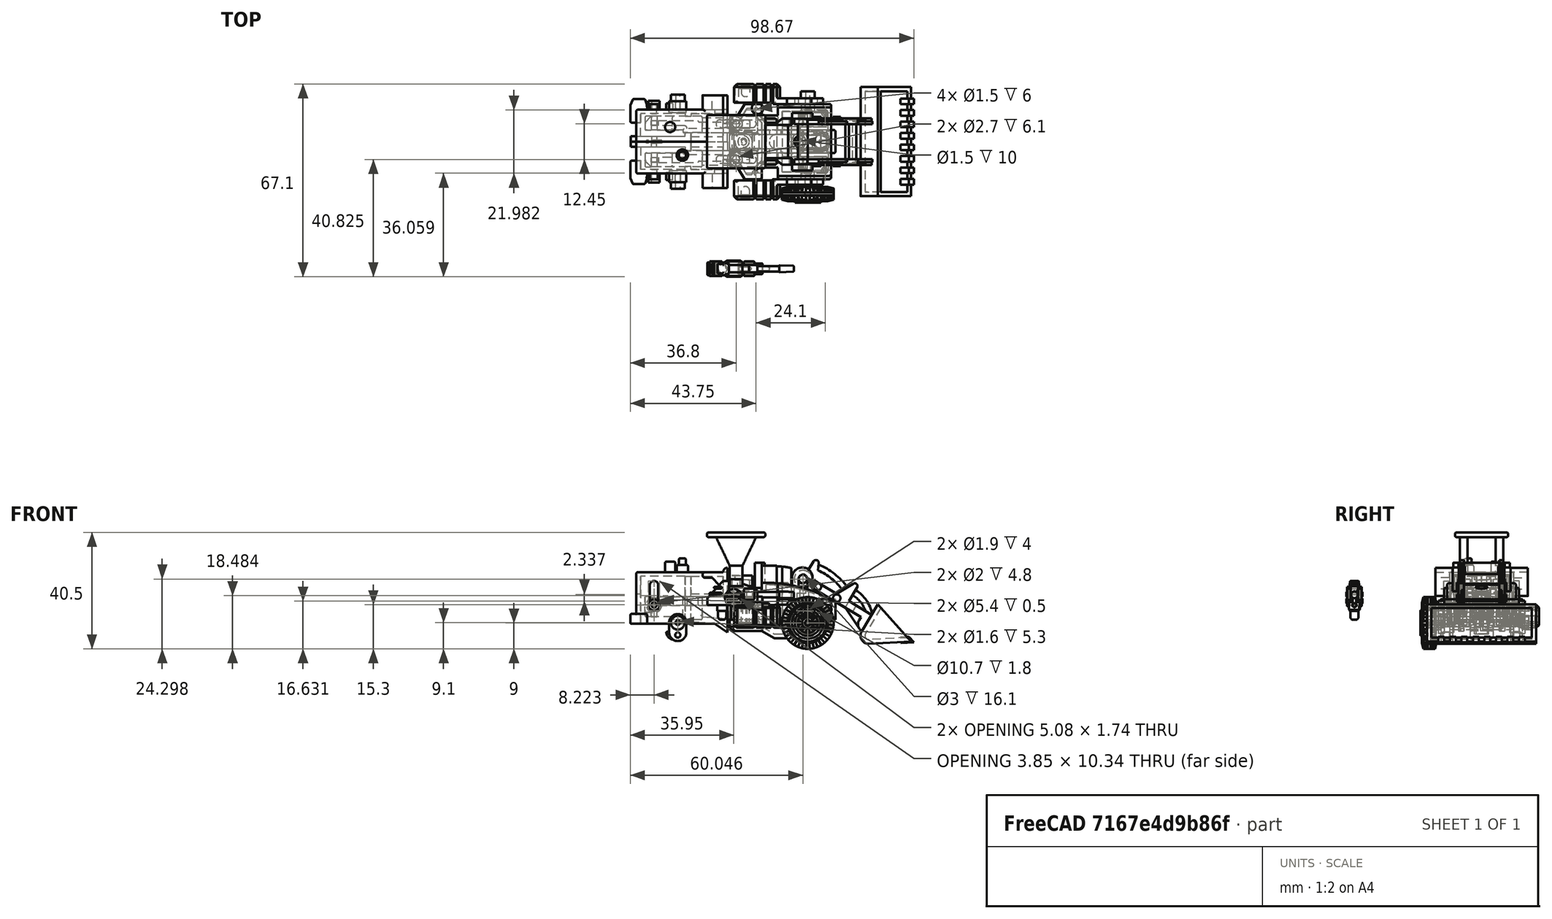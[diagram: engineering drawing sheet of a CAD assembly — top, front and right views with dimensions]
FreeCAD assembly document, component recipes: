
FREECAD ASSEMBLY — COMPONENT RECIPES ("Scrapper")

This assembly document has 14 components, labeled P0..P13 below (a component is one placed body or linked part). 14 of them carry a construction recipe — the FreeCAD feature program that regenerates the part from scratch, quoted from this document or its linked companion documents; the rest are supplied as boundary geometry only. No exploded tour is included for this assembly.
NOTE — document 3 of 4 of this assembly tour. The two overview renders and the header above are repeated from document 1; the component sections below continue where the previous document stopped.
COMPONENT P9 — recipe-attached ("Pre_Left_Arm", modeled in this document).
Construction recipe (the document's own serialized feature program — sketch geometry with constraints, then the solid features built on it; lengths are millimeters unless a unit is written):

FEATURE [Sketcher::SketchObject] Sketch077
  ArcFitTolerance = 1e-06
  AttachmentSupport = -> [XY_Plane002]
  FullyConstrained = true
  MakeInternals = false
  MapMode = 5
  sketch-geometry (20):
    g0: ArcOfCircle CenterX=-3.3 CenterY=1.7225 CenterZ=0 NormalX=0 NormalY=0 NormalZ=1 AngleXU=0 Radius=3.7225 StartAngle=3.62266 EndAngle=5.80212
    g1: ArcOfCircle CenterX=-6.6 CenterY=2 CenterZ=0 NormalX=0 NormalY=0 NormalZ=1 AngleXU=0 Radius=2 StartAngle=3.14159 EndAngle=4.71239
    g2: LineSegment StartX=-8.6 StartY=2 StartZ=0 EndX=-8.6 EndY=6 EndZ=0
    g3: ArcOfCircle CenterX=-6.6 CenterY=6 CenterZ=0 NormalX=0 NormalY=0 NormalZ=1 AngleXU=0 Radius=2 StartAngle=1.5708 EndAngle=3.14159
    g4: LineSegment StartX=-6.6 StartY=8 StartZ=0 EndX=-4.5 EndY=8 EndZ=0
    g5: LineSegment StartX=-4.5 StartY=8 StartZ=0 EndX=-4.5 EndY=8 EndZ=0
    g6: ArcOfCircle CenterX=-3 CenterY=8 CenterZ=0 NormalX=0 NormalY=0 NormalZ=1 AngleXU=0 Radius=1.5 StartAngle=1.5708 EndAngle=3.14159
    g7: LineSegment StartX=-3 StartY=9.5 StartZ=0 EndX=2.4 EndY=9.5 EndZ=0
    g8: ArcOfCircle CenterX=2.4 CenterY=8 CenterZ=0 NormalX=0 NormalY=0 NormalZ=1 AngleXU=0 Radius=1.5 StartAngle=0 EndAngle=1.5708
    g9: LineSegment StartX=3.9 StartY=8 StartZ=0 EndX=8.05 EndY=8 EndZ=0
    g10: ArcOfCircle CenterX=8.05 CenterY=7.25 CenterZ=0 NormalX=0 NormalY=0 NormalZ=1 AngleXU=0 Radius=0.75 StartAngle=4.71239 EndAngle=7.85398
    g11: LineSegment StartX=8.05 StartY=6.5 StartZ=0 EndX=8.05 EndY=1.5 EndZ=0
    g12: ArcOfCircle CenterX=8.05 CenterY=0.75 CenterZ=0 NormalX=0 NormalY=0 NormalZ=1 AngleXU=0 Radius=0.75 StartAngle=4.71239 EndAngle=7.85398
    g13: LineSegment StartX=8.05 StartY=0 StartZ=0 EndX=0 EndY=0 EndZ=0
    g14: LineSegment [constr] StartX=0 StartY=0 StartZ=0 EndX=0 EndY=-2 EndZ=0
    g15: LineSegment [constr] StartX=0 StartY=-2 StartZ=0 EndX=-6.6 EndY=-2 EndZ=0
    g16: LineSegment [constr] StartX=-6.6 StartY=0 StartZ=0 EndX=-6.6 EndY=-2 EndZ=0
    g17: LineSegment [constr] StartX=8.05 StartY=0 StartZ=0 EndX=8.8 EndY=0 EndZ=0
    g18: LineSegment [constr] StartX=8.8 StartY=0 StartZ=0 EndX=8.8 EndY=1.5 EndZ=0
    g19: LineSegment [constr] StartX=8.05 StartY=1.5 StartZ=0 EndX=8.8 EndY=1.5 EndZ=0
  constraints (65):
    c: Coincident(g0,g-1)
    c: PointOnObject(g0,g-1)
    c: Coincident(g1,g0)
    c: Coincident(g2,g1)
    c: Vertical(g2)
    c: Coincident(g3,g2)
    c: Coincident(g4,g3)
    c: Horizontal(g4)
    c: Coincident(g5,g4)
    c: Vertical(g5)
    c: Coincident(g6,g5)
    c: Coincident(g7,g6)
    c: Horizontal(g7)
    c: Coincident(g8,g7)
    c: Coincident(g9,g8)
    c: Horizontal(g9)
    c: Coincident(g10,g9)
    c: Coincident(g11,g10)
    c: Vertical(g11)
    c: Coincident(g12,g11)
    c: PointOnObject(g12,g-1)
    c: Coincident(g13,g12)
    c: Coincident(g13,g0)
    c: Diameter(g10) = 1.5
    c: Diameter(g12) = 1.5
    c: DistanceX(g11,g12) = 0
    c: DistanceX(g12,g12) = 0
    c: DistanceX(g9,g10) = 0
    c: DistanceX(g10,g10) = 0
    c: DistanceY(g11,g10) = 5
    c: DistanceY(g0,g6) = 9.5
    c: DistanceX(g7,g8) = 0
    c: DistanceY(g8,g8) = 0
    c: DistanceY(g5,g6) = 0
    c: DistanceX(g6,g6) = 0
    c: DistanceX(g0,g0) = 6.6
    c: DistanceX(g3,g3) = 0
    c: DistanceX(g1,g0) = 0
    c: DistanceY(g1,g1) = 0
    c: DistanceY(g3,g2) = 0
    c: DistanceY(g0,g3) = 8
    c: Radius(g6) = 1.5
    c: Radius(g3) = 2
    c: Radius(g1) = 2
    c: Coincident(g14,g0)
    c: PointOnObject(g14,g-2)
    c: Coincident(g15,g14)
    c: Horizontal(g15)
    c: Tangent(g15,g0)
    c: Coincident(g16,g0)
    c: Coincident(g16,g15)
    c: Vertical(g16)
    c: DistanceY(g14,g14) = 2
    c: DistanceX(g4,g8) = 8.4
    c: DistanceX(g2,g4) = 4.1
    c: DistanceX(g1,g11) = 16.65
    c: Coincident(g17,g12)
    c: PointOnObject(g17,g-1)
    c: Coincident(g18,g17)
    c: Coincident(g19,g11)
    c: Coincident(g19,g18)
    c: Horizontal(g19)
    c: Tangent(g18,g12)
    c: Vertical(g18)
    c: DistanceX(g0,g17) = 8.8
FEATURE [PartDesign::Pad] Pad049
  Direction = (0,0,1)
  Length = 2
  Length2 = 10
  Profile = -> Sketch077
  ReferenceAxis = -> Sketch077 [N_Axis]
  Refine = true
  Suppressed = false
  Type = 0
FEATURE [Sketcher::SketchObject] Sketch078
  ArcFitTolerance = 1e-06
  AttachmentSupport = -> [Pad049]
  ExternalGeometry = -> [Pad049]
  FullyConstrained = true
  MakeInternals = false
  MapMode = 5
  Placement = pos=(0,0,0) rot=(1,0,0;3.14159rad)
  sketch-geometry (1):
    g0: Circle CenterX=-3.3 CenterY=-1.7225 CenterZ=0 NormalX=0 NormalY=0 NormalZ=1 AngleXU=0 Radius=2.45
  constraints (2):
    c: Coincident(g0,g-3)
    c: Diameter(g0) = 4.9
FEATURE [PartDesign::Pad] Pad050
  BaseFeature = -> Pad049
  Direction = (0,0,-1)
  Length = 2.5
  Length2 = 10
  Profile = -> Sketch078
  ReferenceAxis = -> Sketch078 [N_Axis]
  Refine = true
  Suppressed = false
  Type = 0
FEATURE [Sketcher::SketchObject] Sketch079
  ArcFitTolerance = 1e-06
  AttachmentSupport = -> [Pad050]
  ExternalGeometry = -> [Pad050]
  FullyConstrained = true
  MakeInternals = false
  MapMode = 5
  Placement = pos=(0,0,-2.5) rot=(1,0,0;3.14159rad)
  sketch-geometry (1):
    g0: Circle CenterX=-3.3 CenterY=-1.7225 CenterZ=0 NormalX=0 NormalY=0 NormalZ=1 AngleXU=0 Radius=0.75
  constraints (2):
    c: Coincident(g0,g-4)
    c: Diameter(g0) = 1.5
FEATURE [PartDesign::Pocket] Pocket038
  BaseFeature = -> Pad050
  Direction = (0,0,1)
  Length = 5
  Length2 = 5
  Profile = -> Sketch079
  ReferenceAxis = -> Sketch079 [N_Axis]
  Refine = true
  Suppressed = false
  Type = 0
FEATURE [Sketcher::SketchObject] Sketch080
  ArcFitTolerance = 1e-06
  AttachmentSupport = -> [Pocket038]
  ExternalGeometry = -> [Pocket038]
  FullyConstrained = true
  MakeInternals = false
  MapMode = 5
  Placement = pos=(0,0,0) rot=(1,0,0;3.14159rad)
  sketch-geometry (8):
    g0: LineSegment StartX=6.35 StartY=-8 StartZ=0 EndX=22.35 EndY=-8 EndZ=0
    g1: LineSegment StartX=22.35 StartY=-8 StartZ=0 EndX=22.35 EndY=0 EndZ=0
    g2: LineSegment StartX=22.35 StartY=0 StartZ=0 EndX=6.35 EndY=0 EndZ=0
    g3: LineSegment StartX=6.35 StartY=0 StartZ=0 EndX=6.35 EndY=-8 EndZ=0
    g4: LineSegment StartX=20.85 StartY=-6.5 StartZ=0 EndX=20.85 EndY=-1.5 EndZ=0
    g5: LineSegment StartX=20.85 StartY=-1.5 StartZ=0 EndX=8.05 EndY=-1.5 EndZ=0
    g6: LineSegment StartX=8.05 StartY=-1.5 StartZ=0 EndX=8.05 EndY=-6.5 EndZ=0
    g7: LineSegment StartX=8.05 StartY=-6.5 StartZ=0 EndX=20.85 EndY=-6.5 EndZ=0
  constraints (24):
    c: Coincident(g0,g1)
    c: Coincident(g1,g2)
    c: Coincident(g2,g3)
    c: Coincident(g3,g0)
    c: Horizontal(g0)
    c: Horizontal(g2)
    c: Vertical(g1)
    c: Vertical(g3)
    c: PointOnObject(g0,g-3)
    c: PointOnObject(g1,g-1)
    c: DistanceX(g0,g0) = 16
    c: DistanceX(g-5,g0) = 14.3
    c: Coincident(g4,g5)
    c: Coincident(g5,g6)
    c: Coincident(g6,g7)
    c: Coincident(g7,g4)
    c: Vertical(g4)
    c: Vertical(g6)
    c: Horizontal(g5)
    c: Horizontal(g7)
    c: DistanceX(g4,g0) = 1.5
    c: DistanceY(g4,g1) = 1.5
    c: DistanceY(g4,g4) = 5
    c: Coincident(g6,g-5)
FEATURE [PartDesign::Pad] Pad051
  BaseFeature = -> Pocket038
  Direction = (0,0,-1)
  Length = 5
  Length2 = 10
  Profile = -> Sketch080
  ReferenceAxis = -> Sketch080 [N_Axis]
  Refine = true
  Suppressed = false
  Type = 0
FEATURE [PartDesign::Pad] Pad052
  BaseFeature = -> Pad051
  Direction = (0,0,-1)
  Length = 1.5
  Length2 = 10
  Profile = -> Sketch080
  ReferenceAxis = -> Sketch080 [N_Axis]
  Refine = true
  Reversed = true
  Suppressed = false
  Type = 0
FEATURE [Sketcher::SketchObject] Sketch081
  ArcFitTolerance = 1e-06
  AttachmentSupport = -> [Pad052]
  ExternalGeometry = -> [Pad052]
  FullyConstrained = true
  MakeInternals = false
  MapMode = 5
  Placement = pos=(0,0,-5) rot=(1,0,0;3.14159rad)
  sketch-geometry (4):
    g0: LineSegment StartX=8.05 StartY=-1.5 StartZ=0 EndX=8.05 EndY=-6.5 EndZ=0
    g1: LineSegment StartX=8.05 StartY=-6.5 StartZ=0 EndX=20.85 EndY=-6.5 EndZ=0
    g2: LineSegment StartX=20.85 StartY=-6.5 StartZ=0 EndX=20.85 EndY=-1.5 EndZ=0
    g3: LineSegment StartX=20.85 StartY=-1.5 StartZ=0 EndX=8.05 EndY=-1.5 EndZ=0
  constraints (10):
    c: Coincident(g0,g1)
    c: Coincident(g1,g2)
    c: Coincident(g2,g3)
    c: Coincident(g3,g0)
    c: Vertical(g0)
    c: Vertical(g2)
    c: Horizontal(g1)
    c: Horizontal(g3)
    c: Coincident(g0,g-5)
    c: Coincident(g1,g-6)
FEATURE [PartDesign::Pad] Pad053
  BaseFeature = -> Pad052
  Direction = (0,0,-1)
  Length = 1.5
  Length2 = 10
  Profile = -> Sketch081
  ReferenceAxis = -> Sketch081 [N_Axis]
  Refine = true
  Reversed = true
  Suppressed = false
  Type = 0
FEATURE [PartDesign::Chamfer] Chamfer
  Angle = 45
  Base = -> Pad053 [Edge11,Edge10,Edge40,Edge38,Edge54,Edge37,Edge36,Edge9]
  BaseFeature = -> Pad053
  ChamferType = 0
  FlipDirection = false
  Refine = true
  Size = 1
  Size2 = 1
  SupportTransform = false
  Suppressed = false
  UseAllEdges = false
FEATURE [Sketcher::SketchObject] Sketch082
  ArcFitTolerance = 1e-06
  AttachmentSupport = -> [Chamfer]
  ExternalGeometry = -> [Chamfer]
  FullyConstrained = true
  MakeInternals = false
  MapMode = 5
  Placement = pos=(0,0,-5) rot=(1,0,0;3.14159rad)
  sketch-geometry (8):
    g0: LineSegment StartX=8.8 StartY=0 StartZ=0 EndX=8.8 EndY=-8 EndZ=0
    g1: LineSegment StartX=8.8 StartY=-8 StartZ=0 EndX=9.6 EndY=-8 EndZ=0
    g2: LineSegment StartX=9.6 StartY=-8 StartZ=0 EndX=9.6 EndY=0 EndZ=0
    g3: LineSegment StartX=9.6 StartY=0 StartZ=0 EndX=8.8 EndY=0 EndZ=0
    g4: LineSegment StartX=11.3 StartY=0 StartZ=0 EndX=11.3 EndY=-8 EndZ=0
    g5: LineSegment StartX=11.3 StartY=-8 StartZ=0 EndX=12.1 EndY=-8 EndZ=0
    g6: LineSegment StartX=12.1 StartY=-8 StartZ=0 EndX=12.1 EndY=0 EndZ=0
    g7: LineSegment StartX=12.1 StartY=0 StartZ=0 EndX=11.3 EndY=0 EndZ=0
  constraints (24):
    c: Coincident(g0,g1)
    c: Coincident(g1,g2)
    c: Coincident(g2,g3)
    c: Coincident(g3,g0)
    c: Vertical(g0)
    c: Vertical(g2)
    c: Horizontal(g1)
    c: Horizontal(g3)
    c: PointOnObject(g0,g-4)
    c: PointOnObject(g1,g-5)
    c: Coincident(g4,g5)
    c: Coincident(g5,g6)
    c: Coincident(g6,g7)
    c: Coincident(g7,g4)
    c: Vertical(g4)
    c: Vertical(g6)
    c: Horizontal(g5)
    c: Horizontal(g7)
    c: PointOnObject(g4,g-4)
    c: PointOnObject(g5,g-5)
    c: DistanceX(g-3,g0) = 2.45
    c: DistanceX(g1,g4) = 1.7
    c: DistanceX(g1,g1) = 0.8
    c: DistanceX(g5,g5) = 0.8
FEATURE [PartDesign::Pocket] Pocket039
  BaseFeature = -> Chamfer
  Direction = (0,0,1)
  Length = 0.75
  Length2 = 5
  Profile = -> Sketch082
  ReferenceAxis = -> Sketch082 [N_Axis]
  Refine = true
  Suppressed = false
  Type = 0
FEATURE [Sketcher::SketchObject] Sketch083
  ArcFitTolerance = 1e-06
  AttachmentSupport = -> [Pocket039]
  ExternalGeometry = -> [Pocket039]
  FullyConstrained = true
  MakeInternals = false
  MapMode = 5
  Placement = pos=(0,0,0) rot=(1,0,0;1.5708rad)
  sketch-geometry (8):
    g0: LineSegment StartX=9.6 StartY=-4.25 StartZ=0 EndX=9.6 EndY=1.5 EndZ=0
    g1: LineSegment StartX=9.6 StartY=1.5 StartZ=0 EndX=8.8 EndY=1.5 EndZ=0
    g2: LineSegment StartX=8.8 StartY=1.5 StartZ=0 EndX=8.8 EndY=-4.25 EndZ=0
    g3: LineSegment StartX=8.8 StartY=-4.25 StartZ=0 EndX=9.6 EndY=-4.25 EndZ=0
    g4: LineSegment StartX=12.1 StartY=-4.25 StartZ=0 EndX=12.1 EndY=1.5 EndZ=0
    g5: LineSegment StartX=12.1 StartY=1.5 StartZ=0 EndX=11.3 EndY=1.5 EndZ=0
    g6: LineSegment StartX=11.3 StartY=1.5 StartZ=0 EndX=11.3 EndY=-4.25 EndZ=0
    g7: LineSegment StartX=11.3 StartY=-4.25 StartZ=0 EndX=12.1 EndY=-4.25 EndZ=0
  constraints (20):
    c: Coincident(g0,g1)
    c: Coincident(g1,g2)
    c: Coincident(g2,g3)
    c: Coincident(g3,g0)
    c: Vertical(g0)
    c: Vertical(g2)
    c: Horizontal(g1)
    c: Coincident(g0,g-4)
    c: PointOnObject(g1,g-3)
    c: Coincident(g4,g5)
    c: Coincident(g5,g6)
    c: Coincident(g6,g7)
    c: Coincident(g7,g4)
    c: Vertical(g4)
    c: Vertical(g6)
    c: Horizontal(g5)
    c: Coincident(g4,g-5)
    c: PointOnObject(g5,g-3)
    c: Coincident(g2,g-4)
    c: Coincident(g6,g-5)
FEATURE [PartDesign::Pocket] Pocket040
  BaseFeature = -> Pocket039
  Direction = (0,1,-2e-16)
  Length = 0.75
  Length2 = 5
  Profile = -> Sketch083
  ReferenceAxis = -> Sketch083 [N_Axis]
  Refine = true
  Suppressed = false
  Type = 0
FEATURE [Sketcher::SketchObject] Sketch084
  ArcFitTolerance = 1e-06
  AttachmentSupport = -> [Pocket040]
  ExternalGeometry = -> [Pocket040]
  FullyConstrained = true
  MakeInternals = false
  MapMode = 5
  Placement = pos=(0,8,0) rot=(0,0.707107,0.707107;3.14159rad)
  sketch-geometry (8):
    g0: LineSegment StartX=-8.8 StartY=-4.25 StartZ=0 EndX=-8.8 EndY=1.5 EndZ=0
    g1: LineSegment StartX=-8.8 StartY=1.5 StartZ=0 EndX=-9.6 EndY=1.5 EndZ=0
    g2: LineSegment StartX=-9.6 StartY=1.5 StartZ=0 EndX=-9.6 EndY=-4.25 EndZ=0
    g3: LineSegment StartX=-9.6 StartY=-4.25 StartZ=0 EndX=-8.8 EndY=-4.25 EndZ=0
    g4: LineSegment StartX=-11.3 StartY=-4.25 StartZ=0 EndX=-11.3 EndY=1.5 EndZ=0
    g5: LineSegment StartX=-11.3 StartY=1.5 StartZ=0 EndX=-12.1 EndY=1.5 EndZ=0
    g6: LineSegment StartX=-12.1 StartY=1.5 StartZ=0 EndX=-12.1 EndY=-4.25 EndZ=0
    g7: LineSegment StartX=-12.1 StartY=-4.25 StartZ=0 EndX=-11.3 EndY=-4.25 EndZ=0
  constraints (20):
    c: Coincident(g0,g1)
    c: Coincident(g1,g2)
    c: Coincident(g2,g3)
    c: Coincident(g3,g0)
    c: Vertical(g0)
    c: Vertical(g2)
    c: Horizontal(g1)
    c: Coincident(g0,g-3)
    c: PointOnObject(g1,g-5)
    c: Coincident(g4,g5)
    c: Coincident(g5,g6)
    c: Coincident(g6,g7)
    c: Coincident(g7,g4)
    c: Vertical(g4)
    c: Vertical(g6)
    c: Horizontal(g5)
    c: Coincident(g4,g-4)
    c: PointOnObject(g5,g-5)
    c: Coincident(g6,g-4)
    c: Coincident(g2,g-3)
FEATURE [PartDesign::Pocket] Pocket041
  BaseFeature = -> Pocket040
  Direction = (0,-1,2e-16)
  Length = 0.75
  Length2 = 5
  Profile = -> Sketch084
  ReferenceAxis = -> Sketch084 [N_Axis]
  Refine = true
  Suppressed = false
  Type = 0
FEATURE [Sketcher::SketchObject] Sketch085
  ArcFitTolerance = 1e-06
  AttachmentSupport = -> [Pocket041]
  ExternalGeometry = -> [Pocket041]
  FullyConstrained = true
  MakeInternals = false
  MapMode = 5
  Placement = pos=(0,0,1.5) rot=(0,0,1;0rad)
  sketch-geometry (6):
    g0: ArcOfCircle CenterX=8.05 CenterY=7.25 CenterZ=0 NormalX=0 NormalY=0 NormalZ=1 AngleXU=0 Radius=0.75 StartAngle=5.35e-14 EndAngle=1.5708
    g1: LineSegment StartX=8.05 StartY=8 StartZ=0 EndX=8.8 EndY=8 EndZ=0
    g2: LineSegment StartX=8.8 StartY=8 StartZ=0 EndX=8.8 EndY=7.25 EndZ=0
    g3: ArcOfCircle CenterX=8.05001 CenterY=0.749994 CenterZ=0 NormalX=0 NormalY=0 NormalZ=1 AngleXU=0 Radius=0.749994 StartAngle=4.71238 EndAngle=6.28319
    g4: LineSegment StartX=8.05 StartY=0 StartZ=0 EndX=8.8 EndY=0 EndZ=0
    g5: LineSegment StartX=8.8 StartY=0 StartZ=0 EndX=8.8 EndY=0.75 EndZ=0
  constraints (13):
    c: Tangent(g0,g-5) = -1.5708
    c: Coincident(g0,g-5)
    c: Coincident(g1,g0)
    c: Coincident(g1,g-4)
    c: Coincident(g2,g1)
    c: Coincident(g2,g0)
    c: Coincident(g3,g-8)
    c: Coincident(g3,g-7)
    c: Tangent(g3,g-6)
    c: Coincident(g4,g-8)
    c: Coincident(g5,g4)
    c: Coincident(g5,g-7)
    c: Coincident(g4,g-8)
FEATURE [PartDesign::Pocket] Pocket042
  BaseFeature = -> Pocket041
  Direction = (0,0,-1)
  Length = 7
  Length2 = 5
  Profile = -> Sketch085
  ReferenceAxis = -> Sketch085 [N_Axis]
  Refine = true
  Suppressed = false
  Type = 0
FEATURE [Sketcher::SketchObject] Sketch086
  ArcFitTolerance = 1e-06
  AttachmentSupport = -> [Pocket042]
  ExternalGeometry = -> [Pocket042]
  FullyConstrained = true
  MakeInternals = false
  MapMode = 5
  Placement = pos=(0,0,1.5) rot=(0,0,1;0rad)
  sketch-geometry (6):
    g0: LineSegment StartX=14.6 StartY=0 StartZ=0 EndX=15.1 EndY=0.75 EndZ=0
    g1: LineSegment StartX=15.1 StartY=0.75 StartZ=0 EndX=15.6 EndY=0 EndZ=0
    g2: LineSegment StartX=15.6 StartY=0 StartZ=0 EndX=14.6 EndY=0 EndZ=0
    g3: LineSegment StartX=14.6 StartY=8 StartZ=0 EndX=15.1 EndY=7.25 EndZ=0
    g4: LineSegment StartX=15.1 StartY=7.25 StartZ=0 EndX=15.6 EndY=8 EndZ=0
    g5: LineSegment StartX=15.6 StartY=8 StartZ=0 EndX=14.6 EndY=8 EndZ=0
  constraints (19):
    c: PointOnObject(g0,g-3)
    c: Coincident(g1,g0)
    c: PointOnObject(g1,g-3)
    c: Coincident(g2,g1)
    c: Coincident(g2,g0)
    c: DistanceX(g-3,g0) = 3
    c: DistanceY(g-4,g-4) = 0.75
    c: DistanceY(g0,g0) = 0.75
    c: DistanceX(g2,g2) = 1
    c: DistanceX(g0,g1) = 0.5
    c: PointOnObject(g3,g-5)
    c: Coincident(g4,g3)
    c: PointOnObject(g4,g-5)
    c: Coincident(g5,g4)
    c: Coincident(g5,g3)
    c: DistanceX(g-6,g3) = 3
    c: DistanceX(g5,g5) = 1
    c: DistanceY(g3,g4) = 0.75
    c: DistanceX(g3,g3) = 0.5
FEATURE [PartDesign::Pocket] Pocket043
  BaseFeature = -> Pocket042
  Direction = (0,0,-1)
  Length = 10
  Length2 = 5
  Profile = -> Sketch086
  ReferenceAxis = -> Sketch086 [N_Axis]
  Refine = true
  Suppressed = false
  Type = 0
FEATURE [Sketcher::SketchObject] Sketch087
  ArcFitTolerance = 1e-06
  AttachmentSupport = -> [Pocket043]
  ExternalGeometry = -> [Pocket043]
  FullyConstrained = true
  MakeInternals = false
  MapMode = 5
  Placement = pos=(0,8,0) rot=(0,0.707107,0.707107;3.14159rad)
  sketch-geometry (3):
    g0: LineSegment StartX=-14.6 StartY=-5 StartZ=0 EndX=-15.1 EndY=-4.25 EndZ=0
    g1: LineSegment StartX=-15.1 StartY=-4.25 StartZ=0 EndX=-15.6 EndY=-5 EndZ=0
    g2: LineSegment StartX=-15.6 StartY=-5 StartZ=0 EndX=-14.6 EndY=-5 EndZ=0
  constraints (9):
    c: PointOnObject(g0,g-3)
    c: PointOnObject(g0,g-6)
    c: Coincident(g1,g0)
    c: PointOnObject(g1,g-3)
    c: Coincident(g2,g1)
    c: Coincident(g2,g0)
    c: DistanceX(g2,g2) = 1
    c: DistanceX(g1,g-5) = 0
    c: DistanceY(g0,g0) = 0.75
FEATURE [PartDesign::Pocket] Pocket044
  BaseFeature = -> Pocket043
  Direction = (0,-1,2e-16)
  Length = 8
  Length2 = 5
  Profile = -> Sketch087
  ReferenceAxis = -> Sketch087 [N_Axis]
  Refine = true
  Suppressed = false
  Type = 0
FEATURE [Sketcher::SketchObject] Sketch088
  ArcFitTolerance = 1e-06
  AttachmentSupport = -> [Pocket044]
  ExternalGeometry = -> [Pocket044]
  FullyConstrained = true
  MakeInternals = false
  MapMode = 5
  Placement = pos=(0,0,0) rot=(1,0,0;1.5708rad)
  sketch-geometry (4):
    g0: LineSegment StartX=19.85 StartY=-5 StartZ=0 EndX=16.95 EndY=-5 EndZ=0
    g1: LineSegment StartX=16.95 StartY=-5 StartZ=0 EndX=16.95 EndY=-2.05 EndZ=0
    g2: LineSegment StartX=19.85 StartY=-5 StartZ=0 EndX=19.85 EndY=-2.05 EndZ=0
    g3: ArcOfCircle CenterX=18.4 CenterY=-2.05 CenterZ=0 NormalX=0 NormalY=0 NormalZ=1 AngleXU=0 Radius=1.45 StartAngle=0 EndAngle=3.14159
  constraints (13):
    c: PointOnObject(g0,g-3)
    c: PointOnObject(g0,g-3)
    c: Coincident(g1,g0)
    c: Vertical(g1)
    c: Coincident(g2,g0)
    c: Vertical(g2)
    c: Coincident(g3,g2)
    c: Coincident(g3,g1)
    c: DistanceX(g0,g-4) = 2.5
    c: Radius(g3) = 1.45
    c: DistanceY(g0,g3) = 2.95
    c: DistanceY(g3,g1) = 0
    c: DistanceY(g3,g2) = 0
FEATURE [PartDesign::Pocket] Pocket045
  BaseFeature = -> Pocket044
  Direction = (0,1,-2e-16)
  Length = 1.5
  Length2 = 5
  Profile = -> Sketch088
  ReferenceAxis = -> Sketch088 [N_Axis]
  Refine = true
  Suppressed = false
  Type = 0
FEATURE [Sketcher::SketchObject] Sketch089
  ArcFitTolerance = 1e-06
  AttachmentSupport = -> [Pocket045]
  ExternalGeometry = -> [Pocket045]
  FullyConstrained = true
  MakeInternals = false
  MapMode = 5
  Placement = pos=(22.35,0,0) rot=(0.57735,0.57735,0.57735;2.0944rad)
  sketch-geometry (12):
    g0: LineSegment StartX=1.85 StartY=1.5 StartZ=0 EndX=1.85 EndY=-5 EndZ=0
    g1: LineSegment StartX=1.85 StartY=-5 StartZ=0 EndX=2.05 EndY=-5 EndZ=0
    g2: LineSegment StartX=2.05 StartY=-5 StartZ=0 EndX=2.05 EndY=1.5 EndZ=0
    g3: LineSegment StartX=2.05 StartY=1.5 StartZ=0 EndX=1.85 EndY=1.5 EndZ=0
    g4: LineSegment StartX=3.9 StartY=1.5 StartZ=0 EndX=3.9 EndY=-5 EndZ=0
    g5: LineSegment StartX=3.9 StartY=-5 StartZ=0 EndX=4.1 EndY=-5 EndZ=0
    g6: LineSegment StartX=4.1 StartY=-5 StartZ=0 EndX=4.1 EndY=1.5 EndZ=0
    g7: LineSegment StartX=4.1 StartY=1.5 StartZ=0 EndX=3.9 EndY=1.5 EndZ=0
    g8: LineSegment StartX=5.95 StartY=1.5 StartZ=0 EndX=5.95 EndY=-5 EndZ=0
    g9: LineSegment StartX=5.95 StartY=-5 StartZ=0 EndX=6.15 EndY=-5 EndZ=0
    g10: LineSegment StartX=6.15 StartY=-5 StartZ=0 EndX=6.15 EndY=1.5 EndZ=0
    g11: LineSegment StartX=6.15 StartY=1.5 StartZ=0 EndX=5.95 EndY=1.5 EndZ=0
  constraints (38):
    c: DistanceX(g-4,g-3) = 8
    c: Coincident(g0,g1)
    c: Coincident(g1,g2)
    c: Coincident(g2,g3)
    c: Coincident(g3,g0)
    c: Vertical(g0)
    c: Vertical(g2)
    c: Horizontal(g1)
    c: Horizontal(g3)
    c: PointOnObject(g0,g-5)
    c: PointOnObject(g1,g-6)
    c: Coincident(g4,g5)
    c: Coincident(g5,g6)
    c: Coincident(g6,g7)
    c: Coincident(g7,g4)
    c: Vertical(g4)
    c: Vertical(g6)
    c: Horizontal(g5)
    c: Horizontal(g7)
    c: PointOnObject(g4,g-5)
    c: PointOnObject(g5,g-6)
    c: Coincident(g8,g9)
    c: Coincident(g9,g10)
    c: Coincident(g10,g11)
    c: Coincident(g11,g8)
    c: Vertical(g8)
    c: Vertical(g10)
    c: Horizontal(g9)
    c: Horizontal(g11)
    c: PointOnObject(g8,g-5)
    c: PointOnObject(g9,g-6)
    c: DistanceX(g-4,g0) = 1.85
    c: DistanceX(g2,g4) = 1.85
    c: DistanceX(g3,g3) = 0.2
    c: DistanceX(g7,g7) = 0.2
    c: DistanceX(g11,g11) = 0.2
    c: DistanceX(g6,g8) = 1.85
    c: DistanceX(g10,g-3) = 1.85
FEATURE [PartDesign::Pocket] Pocket046
  BaseFeature = -> Pocket045
  Direction = (-1,0,0)
  Length = 0.3
  Length2 = 5
  Profile = -> Sketch089
  ReferenceAxis = -> Sketch089 [N_Axis]
  Refine = true
  Suppressed = false
  Type = 0
FEATURE [PartDesign::Fillet] Fillet005
  Base = -> Pocket046 [Edge32,Edge34,Edge88,Edge93,Edge36,Edge38,Edge96,Edge101,Edge40,Edge42,Edge104,Edge68,Edge109,Edge106,Edge102,Edge98,Edge94,Edge90]
  BaseFeature = -> Pocket046
  Radius = 0.2
  Refine = true
  SupportTransform = false
  Suppressed = false
  UseAllEdges = false
FEATURE [PartDesign::Fillet] Fillet006
  Base = -> Fillet005 [Edge19,Edge11,Edge5,Edge40,Edge46,Edge39]
  BaseFeature = -> Fillet005
  Radius = 0.5
  Refine = true
  SupportTransform = false
  Suppressed = false
  UseAllEdges = false
FEATURE [PartDesign::Fillet] Fillet007
  Base = -> Fillet006 [Edge1,Edge3,Edge15,Edge27,Edge39,Edge41]
  BaseFeature = -> Fillet006
  Radius = 0.19
  Refine = true
  SupportTransform = false
  Suppressed = false
  UseAllEdges = false
FEATURE [Sketcher::SketchObject] Sketch090
  ArcFitTolerance = 1e-06
  AttachmentSupport = -> [Fillet007]
  ExternalGeometry = -> [Fillet007]
  FullyConstrained = true
  MakeInternals = false
  MapMode = 5
  Placement = pos=(0,0,2) rot=(0,0,1;0rad)
  sketch-geometry (3):
    g0: Circle CenterX=-3.3 CenterY=5.9 CenterZ=0 NormalX=0 NormalY=0 NormalZ=1 AngleXU=0 Radius=2.2
    g1: LineSegment [constr] StartX=-5.5 StartY=8 StartZ=0 EndX=-5.5 EndY=4 EndZ=0
    g2: LineSegment [constr] StartX=-5.5 StartY=8.1 StartZ=0 EndX=0.5 EndY=8.1 EndZ=0
  constraints (11):
    c: Diameter(g0) = 4.4
    c: Vertical(g1)
    c: PointOnObject(g1,g-4)
    c: DistanceY(g1,g1) = 4
    c: Tangent(g1,g0)
    c: PointOnObject(g2,g1)
    c: Horizontal(g2)
    c: DistanceY(g2,g-5) = 1.4
    c: DistanceX(g2,g2) = 6
    c: Tangent(g0,g2)
    c: DistanceX(g0,g-7) = 0
FEATURE [PartDesign::Pad] Pad054
  BaseFeature = -> Fillet007
  Direction = (0,0,1)
  Length = 5.5
  Length2 = 10
  Profile = -> Sketch090
  ReferenceAxis = -> Sketch090 [N_Axis]
  Refine = true
  Suppressed = false
  Type = 0
FEATURE [Sketcher::SketchObject] Sketch091
  ArcFitTolerance = 1e-06
  AttachmentSupport = -> [Pad054]
  ExternalGeometry = -> [Pad054]
  FullyConstrained = true
  MakeInternals = false
  MapMode = 5
  Placement = pos=(0,0,7.5) rot=(0,0,1;0rad)
  sketch-geometry (1):
    g0: Circle CenterX=-3.3 CenterY=5.9 CenterZ=0 NormalX=0 NormalY=0 NormalZ=1 AngleXU=0 Radius=0.95
  constraints (2):
    c: Coincident(g0,g-3)
    c: Diameter(g0) = 1.9
FEATURE [PartDesign::Pocket] Pocket047
  BaseFeature = -> Pad054
  Direction = (0,0,-1)
  Length = 5.5
  Length2 = 5
  Profile = -> Sketch091
  ReferenceAxis = -> Sketch091 [N_Axis]
  Refine = true
  Suppressed = false
  Type = 0
FEATURE [Sketcher::SketchObject] Sketch092
  ArcFitTolerance = 1e-06
  AttachmentOffset = pos=(0,0,-1.6) rot=(0,0,1;0rad)
  AttachmentSupport = -> [Pocket047]
  ExternalGeometry = -> [Pocket047]
  FullyConstrained = true
  MakeInternals = false
  MapMode = 5
  Placement = pos=(0,0,5.9) rot=(0,0,1;0rad)
  sketch-geometry (4):
    g0: LineSegment StartX=-1.31569 StartY=6.85 StartZ=0 EndX=-1.1 EndY=6.85 EndZ=0
    g1: LineSegment StartX=-1.31569 StartY=4.95 StartZ=0 EndX=-1.1 EndY=4.95 EndZ=0
    g2: ArcOfCircle CenterX=-1.1 CenterY=5.9 CenterZ=0 NormalX=0 NormalY=0 NormalZ=1 AngleXU=0 Radius=0.95 StartAngle=4.71239 EndAngle=7.85398
    g3: ArcOfCircle CenterX=-3.3 CenterY=5.9 CenterZ=0 NormalX=0 NormalY=0 NormalZ=1 AngleXU=0 Radius=2.2 StartAngle=5.83668 EndAngle=6.72969
  constraints (13):
    c: PointOnObject(g0,g-4)
    c: Horizontal(g0)
    c: PointOnObject(g1,g-4)
    c: Horizontal(g1)
    c: Coincident(g2,g0)
    c: Coincident(g2,g1)
    c: DistanceX(g2,g2) = 0
    c: DistanceX(g1,g2) = 0
    c: Diameter(g2) = 1.9
    c: Coincident(g3,g0)
    c: Coincident(g3,g1)
    c: PointOnObject(g-3,g3)
    c: Coincident(g2,g-3)
FEATURE [PartDesign::Pad] Pad055
  BaseFeature = -> Pocket047
  Direction = (0,0,1)
  Length = 1.3
  Length2 = 10
  Profile = -> Sketch092
  ReferenceAxis = -> Sketch092 [N_Axis]
  Refine = true
  Reversed = true
  Suppressed = false
  Type = 0
FEATURE [Sketcher::SketchObject] Sketch093
  ArcFitTolerance = 1e-06
  AttachmentSupport = -> [Pad055]
  ExternalGeometry = -> [Pad055]
  FullyConstrained = true
  MakeInternals = false
  MapMode = 5
  Placement = pos=(0,0,2) rot=(0,0,1;0rad)
  sketch-geometry (1):
    g0: Circle CenterX=-0.6 CenterY=5.9 CenterZ=0 NormalX=0 NormalY=0 NormalZ=1 AngleXU=0 Radius=1.8
  constraints (4):
    c: Diameter(g0) = 3.6
    c: Diameter(g-6) = 4.4
    c: DistanceY(g0,g-4) = 0
    c: DistanceX(g-4,g0) = 0.5
FEATURE [PartDesign::Pocket] Pocket048
  BaseFeature = -> Pad055
  Direction = (0,0,-1)
  Length = 5
  Length2 = 5
  Profile = -> Sketch093
  ReferenceAxis = -> Sketch093 [N_Axis]
  Refine = true
  Suppressed = false
  Type = 0
FEATURE [Sketcher::SketchObject] Sketch094
  ArcFitTolerance = 1e-06
  AttachmentSupport = -> [Pocket048]
  ExternalGeometry = -> [Pocket048]
  FullyConstrained = true
  MakeInternals = false
  MapMode = 5
  Placement = pos=(0,0,2) rot=(0,0,1;0rad)
  sketch-geometry (1):
    g0: Circle CenterX=-3.3 CenterY=5.9 CenterZ=0 NormalX=0 NormalY=0 NormalZ=1 AngleXU=0 Radius=0.95
  constraints (2):
    c: Coincident(g0,g-3)
    c: Equal(g0,g-3)
FEATURE [PartDesign::Pad] Pad056
  BaseFeature = -> Pocket048
  Direction = (0,0,1)
  Length = 1.5
  Length2 = 10
  Profile = -> Sketch094
  ReferenceAxis = -> Sketch094 [N_Axis]
  Refine = true
  Suppressed = false
  Type = 0
FEATURE [Sketcher::SketchObject] Sketch095
  ArcFitTolerance = 1e-06
  AttachmentSupport = -> [Pad056]
  ExternalGeometry = -> [Pad056]
  FullyConstrained = true
  MakeInternals = false
  MapMode = 5
  Placement = pos=(0,0,2) rot=(1,0,0;3.14159rad)
  sketch-geometry (4):
    g0: LineSegment StartX=-1.10911 StartY=-6.1 StartZ=0 EndX=-1.05411 EndY=-6.1 EndZ=0
    g1: LineSegment StartX=-1.05411 StartY=-6.1 StartZ=0 EndX=-1.05411 EndY=-5.7 EndZ=0
    g2: LineSegment StartX=-1.05411 StartY=-5.7 StartZ=0 EndX=-1.10911 EndY=-5.7 EndZ=0
    g3: ArcOfCircle CenterX=-3.3 CenterY=-5.9 CenterZ=0 NormalX=0 NormalY=0 NormalZ=1 AngleXU=0 Radius=2.2 StartAngle=6.19215 EndAngle=6.37422
  constraints (13):
    c: PointOnObject(g0,g-4)
    c: Horizontal(g0)
    c: Coincident(g1,g0)
    c: Vertical(g1)
    c: Coincident(g2,g1)
    c: PointOnObject(g2,g-3)
    c: Horizontal(g2)
    c: DistanceY(g-4,g2) = 0.2
    c: DistanceY(g0,g-4) = 0.2
    c: DistanceX(g0,g0) = 0.055
    c: Coincident(g3,g2)
    c: Coincident(g3,g0)
    c: PointOnObject(g-4,g3)
FEATURE [PartDesign::Body] Body002  label="Right_Arm"
  AllowCompound = false
  Group = -> [Sketch077,Pad049,Sketch078,Pad050,Sketch079,Pocket038,Sketch080,Pad051,Pad052,Sketch081,Pad053,Chamfer,Sketch082,Pocket039,Sketch083,Pocket040,Sketch084,Pocket041,Sketch085,Pocket042,Sketch086,Pocket043,Sketch087,Pocket044,Sketch088,Pocket045,Sketch089,Pocket046,Fillet005,Fillet006,Fillet007,Sketch090,Pad054,Sketch091,Pocket047,Sketch092,Pad055,Sketch093,Pocket048,Sketch094,Pad056,Sketch095,+13 more]
  Origin = -> Origin002
  Placement = pos=(-11.4,-15.05,-7.9) rot=(0,-0.71,-0.71;3.14159rad)
  Tip = -> Pocket141
COMPONENT P10 — recipe-attached ("Tire2", modeled in this document).
Construction recipe (the document's own serialized feature program — sketch geometry with constraints, then the solid features built on it; lengths are millimeters unless a unit is written):

FEATURE [Sketcher::SketchObject] Sketch235
  ArcFitTolerance = 1e-06
  AttachmentSupport = -> [XZ_Plane007]
  FullyConstrained = true
  MakeInternals = false
  MapMode = 5
  Placement = pos=(0,0,0) rot=(1,0,0;1.5708rad)
  sketch-geometry (1):
    g0: Circle CenterX=0 CenterY=0 CenterZ=0 NormalX=0 NormalY=0 NormalZ=1 AngleXU=0 Radius=4.5
  constraints (2):
    c: Coincident(g0,g-1)
    c: Diameter(g0) = 9
FEATURE [PartDesign::Pad] Pad145
  Direction = (0,-1,2e-16)
  Length = 5.5
  Length2 = 10
  Placement = pos=(0,0,0) rot=(1,0,0;1.5708rad)
  Profile = -> Sketch235
  ReferenceAxis = -> Sketch235 [N_Axis]
  Refine = true
  Suppressed = false
  Type = 0
FEATURE [Sketcher::SketchObject] Sketch236
  ArcFitTolerance = 1e-06
  AttachmentSupport = -> [Pad145]
  FullyConstrained = true
  MakeInternals = false
  MapMode = 5
  Placement = pos=(0,-5.5,0) rot=(1,0,0;1.5708rad)
  sketch-geometry (1):
    g0: Circle CenterX=0 CenterY=0 CenterZ=0 NormalX=0 NormalY=0 NormalZ=1 AngleXU=0 Radius=3.5
  constraints (2):
    c: Coincident(g0,g-1)
    c: Diameter(g0) = 7
FEATURE [PartDesign::Pocket] Pocket097
  BaseFeature = -> Pad145
  Direction = (0,1,-2e-16)
  Length = 0.5
  Length2 = 5
  Placement = pos=(0,0,0) rot=(1,0,0;1.5708rad)
  Profile = -> Sketch236
  ReferenceAxis = -> Sketch236 [N_Axis]
  Refine = true
  Suppressed = false
  Type = 0
FEATURE [Sketcher::SketchObject] Sketch237
  ArcFitTolerance = 1e-06
  AttachmentSupport = -> [Pocket097]
  FullyConstrained = true
  MakeInternals = false
  MapMode = 5
  Placement = pos=(0,-5,1.4e-15) rot=(1,0,0;1.5708rad)
  sketch-geometry (1):
    g0: Circle CenterX=0 CenterY=0 CenterZ=0 NormalX=0 NormalY=0 NormalZ=1 AngleXU=0 Radius=0.75
  constraints (2):
    c: Coincident(g0,g-1)
    c: Diameter(g0) = 1.5
FEATURE [PartDesign::Pocket] Pocket098
  BaseFeature = -> Pocket097
  Direction = (0,1,-2e-16)
  Length = 5
  Length2 = 5
  Placement = pos=(0,0,0) rot=(1,0,0;1.5708rad)
  Profile = -> Sketch237
  ReferenceAxis = -> Sketch237 [N_Axis]
  Refine = true
  Suppressed = false
  Type = 0
FEATURE [Sketcher::SketchObject] Sketch238
  ArcFitTolerance = 1e-06
  AttachmentSupport = -> [Pocket098]
  FullyConstrained = true
  MakeInternals = false
  MapMode = 5
  Placement = pos=(0,-5,1.4e-15) rot=(1,0,0;1.5708rad)
  sketch-geometry (1):
    g0: Circle CenterX=0 CenterY=0 CenterZ=0 NormalX=0 NormalY=0 NormalZ=1 AngleXU=0 Radius=2
  constraints (2):
    c: Coincident(g0,g-1)
    c: Diameter(g0) = 4
FEATURE [PartDesign::Pocket] Pocket099
  BaseFeature = -> Pocket098
  Direction = (0,1,-2e-16)
  Length = 1.5
  Length2 = 5
  Placement = pos=(0,0,0) rot=(1,0,0;1.5708rad)
  Profile = -> Sketch238
  ReferenceAxis = -> Sketch238 [N_Axis]
  Refine = true
  Suppressed = false
  Type = 0
FEATURE [Sketcher::SketchObject] Sketch239
  ArcFitTolerance = 1e-06
  AttachmentSupport = -> [Pocket099]
  FullyConstrained = true
  MakeInternals = false
  MapMode = 5
  Placement = pos=(0,-5,1.4e-15) rot=(1,0,0;1.5708rad)
  sketch-geometry (12):
    g0: Circle CenterX=0 CenterY=2.75 CenterZ=0 NormalX=0 NormalY=0 NormalZ=1 AngleXU=0 Radius=0.5
    g1: Circle CenterX=2.75 CenterY=0 CenterZ=0 NormalX=0 NormalY=0 NormalZ=1 AngleXU=0 Radius=0.5
    g2: Circle CenterX=0 CenterY=-2.75 CenterZ=0 NormalX=0 NormalY=0 NormalZ=1 AngleXU=0 Radius=0.5
    g3: Circle CenterX=-2.75 CenterY=0 CenterZ=0 NormalX=0 NormalY=0 NormalZ=1 AngleXU=0 Radius=0.5
    g4: Circle CenterX=-1.94454 CenterY=1.94454 CenterZ=0 NormalX=0 NormalY=0 NormalZ=1 AngleXU=0 Radius=0.5
    g5: Circle CenterX=1.94454 CenterY=1.94454 CenterZ=0 NormalX=0 NormalY=0 NormalZ=1 AngleXU=0 Radius=0.5
    g6: Circle CenterX=1.94454 CenterY=-1.94454 CenterZ=0 NormalX=0 NormalY=0 NormalZ=1 AngleXU=0 Radius=0.5
    g7: Circle CenterX=-1.94454 CenterY=-1.94454 CenterZ=0 NormalX=0 NormalY=0 NormalZ=1 AngleXU=0 Radius=0.5
    g8: LineSegment [constr] StartX=0 StartY=0 StartZ=0 EndX=-1.94454 EndY=1.94454 EndZ=0
    g9: LineSegment [constr] StartX=0 StartY=0 StartZ=0 EndX=1.94454 EndY=1.94454 EndZ=0
    g10: LineSegment [constr] StartX=0 StartY=0 StartZ=0 EndX=1.94454 EndY=-1.94454 EndZ=0
    g11: LineSegment [constr] StartX=0 StartY=0 StartZ=0 EndX=-1.94454 EndY=-1.94454 EndZ=0
  constraints (32):
    c: PointOnObject(g0,g-2)
    c: PointOnObject(g1,g-1)
    c: PointOnObject(g2,g-2)
    c: PointOnObject(g3,g-1)
    c: Diameter(g0) = 1
    c: Diameter(g5) = 1
    c: Diameter(g1) = 1
    c: Diameter(g6) = 1
    c: Diameter(g2) = 1
    c: Diameter(g7) = 1
    c: Diameter(g4) = 1
    c: Diameter(g3) = 1
    c: Distance(g-1,g1) = 2.75
    c: Distance(g-1,g0) = 2.75
    c: Distance(g-1,g3) = 2.75
    c: Distance(g-1,g2) = 2.75
    c: Distance(g-1,g6) = 2.75
    c: Distance(g-1,g7) = 2.75
    c: Distance(g-1,g4) = 2.75
    c: Distance(g-1,g5) = 2.75
    c: Coincident(g8,g-1)
    c: Coincident(g8,g4)
    c: Coincident(g9,g8)
    c: Coincident(g9,g5)
    c: Coincident(g10,g8)
    c: Coincident(g10,g6)
    c: Coincident(g11,g8)
    c: Coincident(g11,g7)
    c: Angle(g-2,g8) = 0.785398
    c: Angle(g9,g-2) = 0.785398
    c: Angle(g10,g-1) = 0.785398
    c: Angle(g11,g-1) = 2.35619
FEATURE [PartDesign::Pad] Pad146
  BaseFeature = -> Pocket099
  Direction = (0,-1,2e-16)
  Length = 0.5
  Length2 = 10
  Placement = pos=(0,0,0) rot=(1,0,0;1.5708rad)
  Profile = -> Sketch239
  ReferenceAxis = -> Sketch239 [N_Axis]
  Refine = true
  Suppressed = false
  Type = 0
FEATURE [Sketcher::SketchObject] Sketch240
  ArcFitTolerance = 1e-06
  AttachmentOffset = pos=(0,0,-1) rot=(0,0,1;0rad)
  AttachmentSupport = -> [Pad146]
  ExternalGeometry = -> [Pad146]
  FullyConstrained = true
  MakeInternals = false
  MapMode = 5
  Placement = pos=(0,-4.5,-2e-16) rot=(1,0,0;1.5708rad)
  sketch-geometry (2):
    g0: Circle CenterX=0 CenterY=0 CenterZ=0 NormalX=0 NormalY=0 NormalZ=1 AngleXU=0 Radius=5.5
    g1: Circle CenterX=0 CenterY=0 CenterZ=0 NormalX=0 NormalY=0 NormalZ=1 AngleXU=0 Radius=4.50001
  constraints (4):
    c: Coincident(g0,g-1)
    c: Coincident(g1,g0)
    c: Diameter(g0) = 11
    c: Tangent(g1,g-3)
FEATURE [PartDesign::Pad] Pad147
  BaseFeature = -> Pad146
  Direction = (0,-1,2e-16)
  Length = 4.5
  Length2 = 10
  Placement = pos=(0,0,0) rot=(1,0,0;1.5708rad)
  Profile = -> Sketch240
  ReferenceAxis = -> Sketch240 [N_Axis]
  Refine = true
  Reversed = true
  Suppressed = false
  Type = 0
FEATURE [Sketcher::SketchObject] Sketch241
  ArcFitTolerance = 1e-06
  AttachmentSupport = -> [Pad147]
  ExternalGeometry = -> [Pad147]
  FullyConstrained = true
  MakeInternals = false
  MapMode = 5
  Placement = pos=(0,-5,1.4e-15) rot=(1,0,0;1.5708rad)
  sketch-geometry (2):
    g0: Circle CenterX=0 CenterY=0 CenterZ=0 NormalX=0 NormalY=0 NormalZ=1 AngleXU=0 Radius=5.50001
    g1: Circle CenterX=0 CenterY=0 CenterZ=0 NormalX=0 NormalY=0 NormalZ=1 AngleXU=0 Radius=9
  constraints (4):
    c: Coincident(g0,g-1)
    c: Coincident(g1,g0)
    c: Diameter(g1) = 18
    c: Tangent(g0,g-3)
FEATURE [PartDesign::Pad] Pad148
  BaseFeature = -> Pad147
  Direction = (0,-1,2e-16)
  Length = 5
  Length2 = 10
  Placement = pos=(0,0,0) rot=(1,0,0;1.5708rad)
  Profile = -> Sketch241
  ReferenceAxis = -> Sketch241 [N_Axis]
  Refine = true
  Reversed = true
  Suppressed = false
  Type = 0
FEATURE [Sketcher::SketchObject] Sketch242
  ArcFitTolerance = 1e-06
  AttachmentOffset = pos=(3,0,0) rot=(0,0,1;0rad)
  AttachmentSupport = -> [YZ_Plane007]
  ExternalGeometry = -> [Pad148]
  FullyConstrained = true
  MakeInternals = false
  MapMode = 5
  Placement = pos=(0,3,0) rot=(0.57735,0.57735,0.57735;2.0944rad)
  sketch-geometry (4):
    g0: LineSegment StartX=-8 StartY=6.5 StartZ=0 EndX=-7.5 EndY=5.5 EndZ=0
    g1: LineSegment StartX=-7.5 StartY=5.5 StartZ=0 EndX=-8.5 EndY=5.5 EndZ=0
    g2: LineSegment StartX=-8 StartY=6.5 StartZ=0 EndX=-8.5 EndY=6.5 EndZ=0
    g3: LineSegment StartX=-8.5 StartY=6.5 StartZ=0 EndX=-8.5 EndY=5.5 EndZ=0
  constraints (11):
    c: Coincident(g1,g0)
    c: Horizontal(g1)
    c: Coincident(g0,g-4)
    c: PointOnObject(g0,g-5)
    c: Coincident(g2,g0)
    c: Coincident(g3,g2)
    c: Coincident(g3,g1)
    c: Vertical(g3)
    c: Horizontal(g2)
    c: DistanceY(g0,g0) = 1
    c: DistanceX(g1,g1) = 1
FEATURE [PartDesign::SubtractivePipe] SubtractivePipe
  AuxilleryCurvelinear = true
  AuxillerySpineTangent = false
  BaseFeature = -> Pad148
  Binormal = (0,0,0)
  Mode = 0
  Placement = pos=(0,0,0) rot=(1,0,0;1.5708rad)
  Profile = -> Sketch242
  Refine = true
  Spine = -> Pad148 [Edge6]
  SpineTangent = false
  Suppressed = false
  Transformation = 0
  Transition = 0
FEATURE [PartDesign::Chamfer] Chamfer001
  Angle = 45
  Base = -> SubtractivePipe [Edge10,Edge21]
  BaseFeature = -> SubtractivePipe
  ChamferType = 0
  FlipDirection = false
  Placement = pos=(0,0,0) rot=(1,0,0;1.5708rad)
  Refine = true
  Size = 1.99
  Size2 = 1
  SupportTransform = false
  Suppressed = false
  UseAllEdges = false
FEATURE [Sketcher::SketchObject] Sketch243
  ArcFitTolerance = 1e-06
  AttachmentSupport = -> [Chamfer001]
  ExternalGeometry = -> [Chamfer001]
  FullyConstrained = true
  MakeInternals = false
  MapMode = 5
  Placement = pos=(0,-5,0) rot=(1,0,0;1.5708rad)
  sketch-geometry (120):
    g0: LineSegment [constr] StartX=0 StartY=0 StartZ=0 EndX=-0.706132 EndY=8.97226 EndZ=0
    g1: LineSegment [constr] StartX=0 StartY=0 StartZ=0 EndX=-2.10101 EndY=8.75133 EndZ=0
    g2: LineSegment [constr] StartX=0 StartY=0 StartZ=0 EndX=-3.44415 EndY=8.31492 EndZ=0
    g3: LineSegment [constr] StartX=0 StartY=0 StartZ=0 EndX=-4.70249 EndY=7.67376 EndZ=0
    g4: LineSegment [constr] StartX=0 StartY=0 StartZ=0 EndX=-5.84503 EndY=6.84365 EndZ=0
    g5: LineSegment [constr] StartX=0 StartY=0 StartZ=0 EndX=-6.84365 EndY=5.84503 EndZ=0
    g6: LineSegment [constr] StartX=0 StartY=0 StartZ=0 EndX=-7.67376 EndY=4.70249 EndZ=0
    g7: LineSegment [constr] StartX=0 StartY=0 StartZ=0 EndX=-8.31492 EndY=3.44415 EndZ=0
    g8: LineSegment [constr] StartX=0 StartY=0 StartZ=0 EndX=-8.75133 EndY=2.10101 EndZ=0
    g9: LineSegment [constr] StartX=0 StartY=0 StartZ=0 EndX=-8.97226 EndY=-0.706132 EndZ=0
    g10: LineSegment [constr] StartX=0 StartY=0 StartZ=0 EndX=-8.97226 EndY=0.706132 EndZ=0
    g11: LineSegment [constr] StartX=0 StartY=0 StartZ=0 EndX=-8.75133 EndY=-2.10101 EndZ=0
    g12: LineSegment [constr] StartX=0 StartY=0 StartZ=0 EndX=-8.31492 EndY=-3.44415 EndZ=0
    g13: LineSegment [constr] StartX=0 StartY=0 StartZ=0 EndX=-7.67376 EndY=-4.70249 EndZ=0
    g14: LineSegment [constr] StartX=0 StartY=0 StartZ=0 EndX=-6.84365 EndY=-5.84503 EndZ=0
    g15: LineSegment [constr] StartX=0 StartY=0 StartZ=0 EndX=-5.84503 EndY=-6.84365 EndZ=0
    g16: LineSegment [constr] StartX=0 StartY=0 StartZ=0 EndX=-4.70249 EndY=-7.67376 EndZ=0
    g17: LineSegment [constr] StartX=0 StartY=0 StartZ=0 EndX=-3.44415 EndY=-8.31492 EndZ=0
    g18: LineSegment [constr] StartX=0 StartY=0 StartZ=0 EndX=-2.10101 EndY=-8.75133 EndZ=0
    g19: LineSegment [constr] StartX=0 StartY=0 StartZ=0 EndX=-0.706132 EndY=-8.97226 EndZ=0
    g20: LineSegment [constr] StartX=0 StartY=0 StartZ=0 EndX=0.706132 EndY=-8.97226 EndZ=0
    g21: LineSegment [constr] StartX=0 StartY=0 StartZ=0 EndX=4.70249 EndY=7.67376 EndZ=0
    g22: LineSegment [constr] StartX=0 StartY=0 StartZ=0 EndX=3.44415 EndY=8.31492 EndZ=0
    g23: LineSegment [constr] StartX=0 StartY=0 StartZ=0 EndX=2.10101 EndY=8.75133 EndZ=0
    g24: LineSegment [constr] StartX=0 StartY=0 StartZ=0 EndX=0.706132 EndY=8.97226 EndZ=0
    g25: LineSegment [constr] StartX=0 StartY=0 StartZ=0 EndX=8.97226 EndY=0.706132 EndZ=0
    g26: LineSegment [constr] StartX=0 StartY=0 StartZ=0 EndX=8.97226 EndY=-0.706132 EndZ=0
    g27: LineSegment [constr] StartX=0 StartY=0 StartZ=0 EndX=8.75133 EndY=-2.10101 EndZ=0
    g28: LineSegment [constr] StartX=0 StartY=0 StartZ=0 EndX=8.31492 EndY=-3.44415 EndZ=0
    g29: LineSegment [constr] StartX=0 StartY=0 StartZ=0 EndX=7.67376 EndY=-4.70249 EndZ=0
    g30: LineSegment [constr] StartX=0 StartY=0 StartZ=0 EndX=6.84365 EndY=-5.84503 EndZ=0
    g31: LineSegment [constr] StartX=0 StartY=0 StartZ=0 EndX=5.84503 EndY=-6.84365 EndZ=0
    g32: LineSegment [constr] StartX=0 StartY=0 StartZ=0 EndX=4.70249 EndY=-7.67376 EndZ=0
    g33: LineSegment [constr] StartX=0 StartY=0 StartZ=0 EndX=3.44415 EndY=-8.31492 EndZ=0
    g34: LineSegment [constr] StartX=0 StartY=0 StartZ=0 EndX=2.10101 EndY=-8.75133 EndZ=0
    g35: LineSegment [constr] StartX=0 StartY=0 StartZ=0 EndX=8.75133 EndY=2.10101 EndZ=0
    g36: LineSegment [constr] StartX=0 StartY=0 StartZ=0 EndX=8.31492 EndY=3.44415 EndZ=0
    g37: LineSegment [constr] StartX=0 StartY=0 StartZ=0 EndX=7.67376 EndY=4.70249 EndZ=0
    g38: LineSegment [constr] StartX=0 StartY=0 StartZ=0 EndX=6.84365 EndY=5.84503 EndZ=0
    g39: LineSegment [constr] StartX=0 StartY=0 StartZ=0 EndX=5.84503 EndY=6.84365 EndZ=0
    g40: LineSegment StartX=-0.706132 StartY=8.97226 StartZ=0 EndX=-2.10101 EndY=8.75133 EndZ=0
    g41: LineSegment StartX=-2.10101 StartY=8.75133 StartZ=0 EndX=-1.63645 EndY=6.81631 EndZ=0
    g42: LineSegment StartX=-1.63645 StartY=6.81631 StartZ=0 EndX=-0.549998 EndY=6.98839 EndZ=0
    g43: LineSegment StartX=-0.549998 StartY=6.98839 StartZ=0 EndX=-0.706132 EndY=8.97226 EndZ=0
    g44: LineSegment StartX=-3.44415 StartY=8.31492 StartZ=0 EndX=-4.70249 EndY=7.67376 EndZ=0
    g45: LineSegment StartX=-4.70249 StartY=7.67376 StartZ=0 EndX=-3.66271 EndY=5.97701 EndZ=0
    g46: LineSegment StartX=-3.66271 StartY=5.97701 StartZ=0 EndX=-2.68261 EndY=6.4764 EndZ=0
    g47: LineSegment StartX=-2.68261 StartY=6.4764 StartZ=0 EndX=-3.44415 EndY=8.31492 EndZ=0
    g48: LineSegment StartX=-5.84503 StartY=6.84365 StartZ=0 EndX=-6.84365 EndY=5.84503 EndZ=0
    g49: LineSegment StartX=-6.84365 StartY=5.84503 StartZ=0 EndX=-5.33045 EndY=4.55263 EndZ=0
    g50: LineSegment StartX=-5.33045 StartY=4.55263 StartZ=0 EndX=-4.55263 EndY=5.33045 EndZ=0
    g51: LineSegment StartX=-4.55263 StartY=5.33045 StartZ=0 EndX=-5.84503 EndY=6.84365 EndZ=0
    g52: LineSegment StartX=-7.67376 StartY=4.70249 StartZ=0 EndX=-8.31492 EndY=3.44415 EndZ=0
    g53: LineSegment StartX=-8.31492 StartY=3.44415 StartZ=0 EndX=-6.4764 EndY=2.68261 EndZ=0
    g54: LineSegment StartX=-6.4764 StartY=2.68261 StartZ=0 EndX=-5.97701 EndY=3.66271 EndZ=0
    g55: LineSegment StartX=-5.97701 StartY=3.66271 StartZ=0 EndX=-7.67376 EndY=4.70249 EndZ=0
    g56: LineSegment StartX=-8.75133 StartY=2.10101 StartZ=0 EndX=-8.97226 EndY=0.706132 EndZ=0
    g57: LineSegment StartX=-8.97226 StartY=0.706132 StartZ=0 EndX=-6.98839 EndY=0.549998 EndZ=0
    g58: LineSegment StartX=-6.98839 StartY=0.549998 StartZ=0 EndX=-6.81631 EndY=1.63645 EndZ=0
    g59: LineSegment StartX=-6.81631 StartY=1.63645 StartZ=0 EndX=-8.75133 EndY=2.10101 EndZ=0
    g60: LineSegment StartX=-8.97226 StartY=-0.706132 StartZ=0 EndX=-8.75133 EndY=-2.10101 EndZ=0
    g61: LineSegment StartX=-8.75133 StartY=-2.10101 StartZ=0 EndX=-6.81631 EndY=-1.63645 EndZ=0
    g62: LineSegment StartX=-6.81631 StartY=-1.63645 StartZ=0 EndX=-6.98839 EndY=-0.549998 EndZ=0
    g63: LineSegment StartX=-6.98839 StartY=-0.549998 StartZ=0 EndX=-8.97226 EndY=-0.706132 EndZ=0
    g64: LineSegment StartX=-8.31492 StartY=-3.44415 StartZ=0 EndX=-7.67376 EndY=-4.70249 EndZ=0
    g65: LineSegment StartX=-7.67376 StartY=-4.70249 StartZ=0 EndX=-5.97701 EndY=-3.66271 EndZ=0
    g66: LineSegment StartX=-5.97701 StartY=-3.66271 StartZ=0 EndX=-6.4764 EndY=-2.68261 EndZ=0
    g67: LineSegment StartX=-6.4764 StartY=-2.68261 StartZ=0 EndX=-8.31492 EndY=-3.44415 EndZ=0
    g68: LineSegment StartX=-6.84365 StartY=-5.84503 StartZ=0 EndX=-5.84503 EndY=-6.84365 EndZ=0
    g69: LineSegment StartX=-5.84503 StartY=-6.84365 StartZ=0 EndX=-4.55263 EndY=-5.33045 EndZ=0
    g70: LineSegment StartX=-4.55263 StartY=-5.33045 StartZ=0 EndX=-5.33045 EndY=-4.55263 EndZ=0
    g71: LineSegment StartX=-5.33045 StartY=-4.55263 StartZ=0 EndX=-6.84365 EndY=-5.84503 EndZ=0
    g72: LineSegment StartX=-4.70249 StartY=-7.67376 StartZ=0 EndX=-3.44415 EndY=-8.31492 EndZ=0
    g73: LineSegment StartX=-3.44415 StartY=-8.31492 StartZ=0 EndX=-2.68261 EndY=-6.4764 EndZ=0
    g74: LineSegment StartX=-2.68261 StartY=-6.4764 StartZ=0 EndX=-3.66271 EndY=-5.97701 EndZ=0
    g75: LineSegment StartX=-3.66271 StartY=-5.97701 StartZ=0 EndX=-4.70249 EndY=-7.67376 EndZ=0
    g76: LineSegment StartX=-2.10101 StartY=-8.75133 StartZ=0 EndX=-1.63645 EndY=-6.81631 EndZ=0
    g77: LineSegment StartX=-1.63645 StartY=-6.81631 StartZ=0 EndX=-0.549998 EndY=-6.98839 EndZ=0
    g78: LineSegment StartX=-0.549998 StartY=-6.98839 StartZ=0 EndX=-0.706132 EndY=-8.97226 EndZ=0
    g79: LineSegment StartX=-0.706132 StartY=-8.97226 StartZ=0 EndX=-2.10101 EndY=-8.75133 EndZ=0
    g80: LineSegment StartX=0.706132 StartY=-8.97226 StartZ=0 EndX=2.10101 EndY=-8.75133 EndZ=0
    g81: LineSegment StartX=2.10101 StartY=-8.75133 StartZ=0 EndX=1.63645 EndY=-6.81631 EndZ=0
    g82: LineSegment StartX=1.63645 StartY=-6.81631 StartZ=0 EndX=0.549998 EndY=-6.98839 EndZ=0
    g83: LineSegment StartX=0.549998 StartY=-6.98839 StartZ=0 EndX=0.706132 EndY=-8.97226 EndZ=0
    g84: LineSegment StartX=3.44415 StartY=-8.31492 StartZ=0 EndX=4.70249 EndY=-7.67376 EndZ=0
    g85: LineSegment StartX=4.70249 StartY=-7.67376 StartZ=0 EndX=3.66271 EndY=-5.97701 EndZ=0
    g86: LineSegment StartX=3.66271 StartY=-5.97701 StartZ=0 EndX=2.68261 EndY=-6.4764 EndZ=0
    g87: LineSegment StartX=2.68261 StartY=-6.4764 StartZ=0 EndX=3.44415 EndY=-8.31492 EndZ=0
    g88: LineSegment StartX=5.84503 StartY=-6.84365 StartZ=0 EndX=6.84365 EndY=-5.84503 EndZ=0
    g89: LineSegment StartX=6.84365 StartY=-5.84503 StartZ=0 EndX=5.33045 EndY=-4.55263 EndZ=0
    g90: LineSegment StartX=5.33045 StartY=-4.55263 StartZ=0 EndX=4.55263 EndY=-5.33045 EndZ=0
    g91: LineSegment StartX=5.84503 StartY=-6.84365 StartZ=0 EndX=4.55263 EndY=-5.33045 EndZ=0
    g92: LineSegment StartX=7.67376 StartY=-4.70249 StartZ=0 EndX=5.97701 EndY=-3.66271 EndZ=0
    g93: LineSegment StartX=7.67376 StartY=-4.70249 StartZ=0 EndX=8.31492 EndY=-3.44415 EndZ=0
    g94: LineSegment StartX=8.31492 StartY=-3.44415 StartZ=0 EndX=6.4764 EndY=-2.68261 EndZ=0
    g95: LineSegment StartX=6.4764 StartY=-2.68261 StartZ=0 EndX=5.97701 EndY=-3.66271 EndZ=0
    g96: LineSegment StartX=8.75133 StartY=-2.10101 StartZ=0 EndX=8.97226 EndY=-0.706132 EndZ=0
    g97: LineSegment StartX=8.97226 StartY=-0.706132 StartZ=0 EndX=6.98839 EndY=-0.549998 EndZ=0
    g98: LineSegment StartX=6.98839 StartY=-0.549998 StartZ=0 EndX=6.81631 EndY=-1.63645 EndZ=0
    g99: LineSegment StartX=8.75133 StartY=-2.10101 StartZ=0 EndX=6.81631 EndY=-1.63645 EndZ=0
    g100: LineSegment StartX=8.97226 StartY=0.706132 StartZ=0 EndX=8.75133 EndY=2.10101 EndZ=0
    g101: LineSegment StartX=8.75133 StartY=2.10101 StartZ=0 EndX=6.81631 EndY=1.63645 EndZ=0
    g102: LineSegment StartX=8.97226 StartY=0.706132 StartZ=0 EndX=6.98839 EndY=0.549998 EndZ=0
    g103: LineSegment StartX=6.98839 StartY=0.549998 StartZ=0 EndX=6.81631 EndY=1.63645 EndZ=0
    g104: LineSegment StartX=8.31492 StartY=3.44415 StartZ=0 EndX=7.67376 EndY=4.70249 EndZ=0
    g105: LineSegment StartX=7.67376 StartY=4.70249 StartZ=0 EndX=5.97701 EndY=3.66271 EndZ=0
    g106: LineSegment StartX=5.97701 StartY=3.66271 StartZ=0 EndX=6.4764 EndY=2.68261 EndZ=0
    g107: LineSegment StartX=6.4764 StartY=2.68261 StartZ=0 EndX=8.31492 EndY=3.44415 EndZ=0
    g108: LineSegment StartX=6.84365 StartY=5.84503 StartZ=0 EndX=5.84503 EndY=6.84365 EndZ=0
    g109: LineSegment StartX=5.84503 StartY=6.84365 StartZ=0 EndX=4.55263 EndY=5.33045 EndZ=0
    g110: LineSegment StartX=6.84365 StartY=5.84503 StartZ=0 EndX=5.33045 EndY=4.55263 EndZ=0
    g111: LineSegment StartX=5.33045 StartY=4.55263 StartZ=0 EndX=4.55263 EndY=5.33045 EndZ=0
    g112: LineSegment StartX=4.70249 StartY=7.67376 StartZ=0 EndX=3.66271 EndY=5.97701 EndZ=0
    g113: LineSegment StartX=4.70249 StartY=7.67376 StartZ=0 EndX=3.44415 EndY=8.31492 EndZ=0
    g114: LineSegment StartX=3.44415 StartY=8.31492 StartZ=0 EndX=2.68261 EndY=6.4764 EndZ=0
    g115: LineSegment StartX=2.68261 StartY=6.4764 StartZ=0 EndX=3.66271 EndY=5.97701 EndZ=0
    g116: LineSegment StartX=0.706132 StartY=8.97226 StartZ=0 EndX=2.10101 EndY=8.75133 EndZ=0
    g117: LineSegment StartX=2.10101 StartY=8.75133 StartZ=0 EndX=1.63645 EndY=6.81631 EndZ=0
    g118: LineSegment StartX=1.63645 StartY=6.81631 StartZ=0 EndX=0.549998 EndY=6.98839 EndZ=0
    g119: LineSegment StartX=0.549998 StartY=6.98839 StartZ=0 EndX=0.706132 EndY=8.97226 EndZ=0
  constraints (320):
    c: Coincident(g0,g-1)
    c: PointOnObject(g0,g-3)
    c: Coincident(g1,g0)
    c: PointOnObject(g1,g-3)
    c: Coincident(g2,g0)
    c: PointOnObject(g2,g-3)
    c: Coincident(g3,g0)
    c: PointOnObject(g3,g-3)
    c: Coincident(g4,g0)
    c: PointOnObject(g4,g-3)
    c: Coincident(g5,g0)
    c: PointOnObject(g5,g-3)
    c: Angle(g-2,g0) = 0.0785398
    c: Angle(g0,g1) = 0.15708
    c: Angle(g1,g2) = 0.15708
    c: Angle(g2,g3) = 0.15708
    c: Angle(g3,g4) = 0.15708
    c: Angle(g4,g5) = 0.15708
    c: Coincident(g6,g0)
    c: PointOnObject(g6,g-3)
    c: Coincident(g7,g0)
    c: PointOnObject(g7,g-3)
    c: Coincident(g8,g0)
    c: PointOnObject(g8,g-3)
    c: Coincident(g9,g0)
    c: PointOnObject(g9,g-3)
    c: Coincident(g10,g0)
    c: PointOnObject(g10,g-3)
    c: Coincident(g11,g0)
    c: PointOnObject(g11,g-3)
    c: Coincident(g12,g0)
    c: PointOnObject(g12,g-3)
    c: Coincident(g13,g0)
    c: PointOnObject(g13,g-3)
    c: Coincident(g14,g0)
    c: PointOnObject(g14,g-3)
    c: Angle(g5,g6) = 0.15708
    c: Angle(g6,g7) = 0.15708
    c: Angle(g7,g8) = 0.15708
    c: Angle(g8,g10) = 0.15708
    c: Angle(g10,g9) = 0.15708
    c: Angle(g9,g11) = 0.15708
    c: Angle(g11,g12) = 0.15708
    c: Angle(g12,g13) = 0.15708
    c: Angle(g13,g14) = 0.15708
    c: Coincident(g15,g0)
    c: PointOnObject(g15,g-3)
    c: Coincident(g16,g0)
    c: PointOnObject(g16,g-3)
    c: Coincident(g17,g0)
    c: PointOnObject(g17,g-3)
    c: Coincident(g18,g0)
    c: PointOnObject(g18,g-3)
    c: Coincident(g19,g0)
    c: PointOnObject(g19,g-3)
    c: Coincident(g20,g0)
    c: PointOnObject(g20,g-3)
    c: Coincident(g21,g0)
    c: PointOnObject(g21,g-3)
    c: Coincident(g22,g0)
    c: PointOnObject(g22,g-3)
    c: Coincident(g23,g0)
    c: PointOnObject(g23,g-3)
    c: Coincident(g24,g0)
    c: PointOnObject(g24,g-3)
    c: Angle(g14,g15) = 0.15708
    c: Angle(g15,g16) = 0.15708
    c: Angle(g16,g17) = 0.15708
    c: Angle(g17,g18) = 0.15708
    c: Angle(g18,g19) = 0.15708
    c: Angle(g19,g20) = 0.15708
    c: Angle(g24,g0) = 0.15708
    c: Angle(g23,g24) = 0.15708
    c: Angle(g22,g23) = 0.15708
    c: Angle(g21,g22) = 0.15708
    c: Coincident(g25,g0)
    c: PointOnObject(g25,g-3)
    c: Coincident(g26,g0)
    c: PointOnObject(g26,g-3)
    c: Coincident(g27,g0)
    c: PointOnObject(g27,g-3)
    c: Coincident(g28,g0)
    c: PointOnObject(g28,g-3)
    c: Coincident(g29,g0)
    c: PointOnObject(g29,g-3)
    c: Coincident(g30,g0)
    c: PointOnObject(g30,g-3)
    c: Coincident(g31,g0)
    c: PointOnObject(g31,g-3)
    c: Coincident(g32,g0)
    c: PointOnObject(g32,g-3)
    c: Coincident(g33,g0)
    c: PointOnObject(g33,g-3)
    c: Coincident(g34,g0)
    c: PointOnObject(g34,g-3)
    c: Angle(g20,g34) = 0.15708
    c: Angle(g34,g33) = 0.15708
    c: Angle(g33,g32) = 0.15708
    c: Angle(g32,g31) = 0.15708
    c: Angle(g31,g30) = 0.15708
    c: Angle(g30,g29) = 0.15708
    c: Angle(g29,g28) = 0.15708
    c: Angle(g28,g27) = 0.15708
    c: Angle(g27,g26) = 0.15708
    c: Angle(g26,g25) = 0.15708
    c: Coincident(g35,g0)
    c: PointOnObject(g35,g-3)
    c: Coincident(g36,g0)
    c: PointOnObject(g36,g-3)
    c: Coincident(g37,g0)
    c: PointOnObject(g37,g-3)
    c: Coincident(g38,g0)
    c: PointOnObject(g38,g-3)
    c: Coincident(g39,g0)
    c: PointOnObject(g39,g-3)
    c: Angle(g25,g35) = 0.15708
    c: Angle(g35,g36) = 0.15708
    c: Angle(g36,g37) = 0.15708
    c: Angle(g37,g38) = 0.15708
    c: Angle(g38,g39) = 0.15708
    c: Coincident(g40,g0)
    c: Coincident(g40,g1)
    c: Coincident(g41,g1)
    c: PointOnObject(g41,g1)
    c: Coincident(g42,g41)
    c: PointOnObject(g42,g0)
    c: Coincident(g43,g42)
    c: Coincident(g43,g0)
    c: PointOnObject(g42,g-4)
    c: PointOnObject(g41,g-4)
    c: Coincident(g44,g2)
    c: Coincident(g45,g44)
    c: PointOnObject(g45,g3)
    c: Coincident(g46,g45)
    c: PointOnObject(g46,g2)
    c: Coincident(g47,g46)
    c: Coincident(g47,g2)
    c: Coincident(g48,g4)
    c: PointOnObject(g49,g5)
    c: Coincident(g50,g49)
    c: PointOnObject(g50,g4)
    c: Coincident(g51,g50)
    c: Coincident(g51,g4)
    c: Coincident(g52,g6)
    c: PointOnObject(g53,g7)
    c: Coincident(g54,g53)
    c: PointOnObject(g54,g6)
    c: Coincident(g55,g54)
    c: Coincident(g55,g6)
    c: Coincident(g56,g8)
    c: PointOnObject(g57,g10)
    c: Coincident(g58,g57)
    c: PointOnObject(g58,g8)
    c: Coincident(g59,g58)
    c: Coincident(g59,g56)
    c: Coincident(g60,g11)
    c: PointOnObject(g61,g11)
    c: Coincident(g62,g61)
    c: PointOnObject(g62,g9)
    c: Coincident(g63,g60)
    c: Coincident(g64,g12)
    c: Coincident(g64,g13)
    c: PointOnObject(g65,g13)
    c: Coincident(g66,g65)
    c: PointOnObject(g66,g12)
    c: Coincident(g67,g66)
    c: Coincident(g67,g12)
    c: Coincident(g68,g14)
    c: Coincident(g68,g15)
    c: Coincident(g69,g68)
    c: PointOnObject(g69,g15)
    c: Coincident(g70,g69)
    c: PointOnObject(g70,g14)
    c: Coincident(g71,g70)
    c: Coincident(g71,g68)
    c: Coincident(g72,g16)
    c: Coincident(g72,g17)
    c: Coincident(g73,g17)
    c: PointOnObject(g73,g17)
    c: Coincident(g74,g73)
    c: PointOnObject(g74,g16)
    c: Coincident(g75,g74)
    c: Coincident(g75,g16)
    c: Coincident(g76,g18)
    c: PointOnObject(g76,g18)
    c: Coincident(g77,g76)
    c: PointOnObject(g77,g19)
    c: Coincident(g78,g77)
    c: Coincident(g78,g19)
    c: Coincident(g79,g78)
    c: Coincident(g79,g18)
    c: PointOnObject(g46,g-4)
    c: PointOnObject(g45,g-4)
    c: Coincident(g44,g3)
    c: PointOnObject(g50,g-4)
    c: PointOnObject(g49,g-4)
    c: Coincident(g48,g5)
    c: Coincident(g49,g5)
    c: PointOnObject(g54,g-4)
    c: PointOnObject(g53,g-4)
    c: Coincident(g53,g52)
    c: Coincident(g53,g7)
    c: PointOnObject(g58,g-4)
    c: PointOnObject(g57,g-4)
    c: Coincident(g57,g56)
    c: Coincident(g56,g10)
    c: Coincident(g60,g9)
    c: Coincident(g61,g11)
    c: PointOnObject(g61,g-4)
    c: Coincident(g63,g62)
    c: PointOnObject(g62,g-4)
    c: PointOnObject(g66,g-4)
    c: PointOnObject(g65,g-4)
    c: Coincident(g65,g13)
    c: PointOnObject(g70,g-4)
    c: PointOnObject(g69,g-4)
    c: PointOnObject(g73,g-4)
    c: PointOnObject(g74,g-4)
    c: PointOnObject(g76,g-4)
    c: PointOnObject(g77,g-4)
    c: Coincident(g80,g20)
    c: Coincident(g80,g34)
    c: Coincident(g81,g34)
    c: PointOnObject(g81,g34)
    c: Coincident(g82,g81)
    c: PointOnObject(g82,g20)
    c: Coincident(g83,g82)
    c: Coincident(g83,g20)
    c: Coincident(g84,g33)
    c: Coincident(g84,g32)
    c: Coincident(g85,g32)
    c: PointOnObject(g85,g32)
    c: Coincident(g86,g85)
    c: PointOnObject(g86,g33)
    c: Coincident(g87,g86)
    c: Coincident(g87,g33)
    c: Coincident(g88,g31)
    c: Coincident(g88,g30)
    c: Coincident(g89,g30)
    c: PointOnObject(g89,g30)
    c: Coincident(g90,g89)
    c: PointOnObject(g90,g31)
    c: Coincident(g91,g31)
    c: Coincident(g91,g90)
    c: Coincident(g92,g29)
    c: PointOnObject(g92,g29)
    c: Coincident(g93,g29)
    c: Coincident(g93,g28)
    c: Coincident(g94,g28)
    c: PointOnObject(g94,g28)
    c: Coincident(g95,g94)
    c: Coincident(g95,g92)
    c: Coincident(g96,g27)
    c: Coincident(g96,g26)
    c: Coincident(g97,g26)
    c: PointOnObject(g97,g26)
    c: Coincident(g98,g97)
    c: PointOnObject(g98,g27)
    c: Coincident(g99,g96)
    c: Coincident(g99,g98)
    c: Coincident(g100,g25)
    c: Coincident(g100,g35)
    c: Coincident(g101,g35)
    c: PointOnObject(g101,g35)
    c: Coincident(g102,g100)
    c: PointOnObject(g102,g25)
    c: Coincident(g103,g102)
    c: Coincident(g103,g101)
    c: Coincident(g104,g36)
    c: Coincident(g104,g37)
    c: Coincident(g105,g37)
    c: PointOnObject(g105,g37)
    c: Coincident(g106,g105)
    c: PointOnObject(g106,g36)
    c: Coincident(g107,g106)
    c: Coincident(g107,g36)
    c: Coincident(g108,g38)
    c: Coincident(g108,g39)
    c: Coincident(g109,g108)
    c: PointOnObject(g109,g39)
    c: Coincident(g110,g38)
    c: PointOnObject(g110,g38)
    c: Coincident(g111,g110)
    c: Coincident(g111,g109)
    c: Coincident(g112,g21)
    c: PointOnObject(g112,g21)
    c: Coincident(g113,g21)
    c: Coincident(g113,g22)
    c: Coincident(g114,g22)
    c: PointOnObject(g114,g22)
    c: Coincident(g115,g114)
    c: Coincident(g115,g112)
    c: Coincident(g116,g24)
    c: Coincident(g116,g23)
    c: Coincident(g117,g23)
    c: PointOnObject(g117,g23)
    c: Coincident(g118,g117)
    c: PointOnObject(g118,g24)
    c: Coincident(g119,g118)
    c: Coincident(g119,g24)
    c: PointOnObject(g118,g-4)
    c: PointOnObject(g117,g-4)
    c: PointOnObject(g114,g-4)
    c: PointOnObject(g112,g-4)
    c: PointOnObject(g109,g-4)
    c: PointOnObject(g110,g-4)
    c: PointOnObject(g105,g-4)
    c: PointOnObject(g106,g-4)
    c: PointOnObject(g101,g-4)
    c: PointOnObject(g102,g-4)
    c: PointOnObject(g97,g-4)
    c: PointOnObject(g98,g-4)
    c: PointOnObject(g94,g-4)
    c: PointOnObject(g92,g-4)
    c: PointOnObject(g89,g-4)
    c: PointOnObject(g90,g-4)
    c: PointOnObject(g85,g-4)
    c: PointOnObject(g86,g-4)
    c: PointOnObject(g81,g-4)
    c: PointOnObject(g82,g-4)
FEATURE [PartDesign::Pad] Pad149
  BaseFeature = -> Chamfer001
  Direction = (0,-1,2e-16)
  Length = 2
  Length2 = 10
  Placement = pos=(0,0,0) rot=(1,0,0;1.5708rad)
  Profile = -> Sketch243
  ReferenceAxis = -> Sketch243 [N_Axis]
  Refine = true
  Reversed = true
  Suppressed = false
  Type = 0
FEATURE [Sketcher::SketchObject] Sketch244
  ArcFitTolerance = 1e-06
  AttachmentSupport = -> [Pad149]
  ExternalGeometry = -> [Pad149]
  FullyConstrained = true
  MakeInternals = false
  MapMode = 5
  Placement = pos=(2e-16,0,0) rot=(0.734323,0,0.678801;3.14159rad)
  sketch-geometry (3):
    g0: LineSegment StartX=-7.01 StartY=5 StartZ=0 EndX=-9 EndY=5 EndZ=0
    g1: LineSegment StartX=-9 StartY=5 StartZ=0 EndX=-9 EndY=4.5 EndZ=0
    g2: LineSegment StartX=-9 StartY=4.5 StartZ=0 EndX=-7.01 EndY=5 EndZ=0
  constraints (7):
    c: Coincident(g0,g-3)
    c: Coincident(g0,g-4)
    c: Coincident(g1,g0)
    c: PointOnObject(g1,g-4)
    c: Coincident(g2,g1)
    c: Coincident(g2,g0)
    c: DistanceY(g1,g1) = 0.5
FEATURE [PartDesign::SubtractivePipe] SubtractivePipe001
  AuxilleryCurvelinear = true
  AuxillerySpineTangent = false
  BaseFeature = -> Pad149
  Binormal = (0,0,0)
  Mode = 0
  Placement = pos=(0,0,0) rot=(1,0,0;1.5708rad)
  Profile = -> Sketch244
  Refine = true
  Spine = -> Pad149 [Edge3]
  SpineTangent = false
  Suppressed = false
  Transformation = 0
  Transition = 0
FEATURE [Sketcher::SketchObject] Sketch245
  ArcFitTolerance = 1e-06
  AttachmentSupport = -> [SubtractivePipe001]
  FullyConstrained = true
  MakeInternals = false
  MapMode = 5
  Placement = pos=(0,0,0) rot=(-1,0,0;1.5708rad)
  sketch-geometry (1):
    g0: Circle CenterX=0 CenterY=0 CenterZ=0 NormalX=0 NormalY=0 NormalZ=1 AngleXU=0 Radius=2.7
  constraints (2):
    c: Coincident(g0,g-1)
    c: Diameter(g0) = 5.4
FEATURE [PartDesign::Pocket] Pocket100
  BaseFeature = -> SubtractivePipe001
  Direction = (0,-1,-2e-16)
  Length = 1.8
  Length2 = 5
  Placement = pos=(0,0,0) rot=(1,0,0;1.5708rad)
  Profile = -> Sketch245
  ReferenceAxis = -> Sketch245 [N_Axis]
  Refine = true
  Suppressed = false
  Type = 0
FEATURE [Sketcher::SketchObject] Sketch246
  ArcFitTolerance = 1e-06
  AttachmentSupport = -> [Pocket100]
  FullyConstrained = true
  MakeInternals = false
  MapMode = 5
  Placement = pos=(0,0,0) rot=(-1,0,0;1.5708rad)
  sketch-geometry (2):
    g0: Circle CenterX=0 CenterY=0 CenterZ=0 NormalX=0 NormalY=0 NormalZ=1 AngleXU=0 Radius=4
    g1: Circle CenterX=0 CenterY=0 CenterZ=0 NormalX=0 NormalY=0 NormalZ=1 AngleXU=0 Radius=5.35
  constraints (4):
    c: Coincident(g0,g-1)
    c: Coincident(g1,g0)
    c: Diameter(g0) = 8
    c: Diameter(g1) = 10.7
FEATURE [PartDesign::Pocket] Pocket101
  BaseFeature = -> Pocket100
  Direction = (0,-1,-2e-16)
  Length = 1.8
  Length2 = 5
  Placement = pos=(0,0,0) rot=(1,0,0;1.5708rad)
  Profile = -> Sketch246
  ReferenceAxis = -> Sketch246 [N_Axis]
  Refine = true
  Suppressed = false
  Type = 0
FEATURE [Sketcher::SketchObject] Sketch247
  ArcFitTolerance = 1e-06
  AttachmentSupport = -> [Pocket101]
  ExternalGeometry = -> [Pocket101]
  FullyConstrained = true
  MakeInternals = false
  MapMode = 5
  Placement = pos=(0,0,0) rot=(-1,0,0;1.5708rad)
  sketch-geometry (120):
    g0: LineSegment [constr] StartX=0 StartY=0 StartZ=0 EndX=0.706132 EndY=8.97226 EndZ=0
    g1: LineSegment [constr] StartX=0 StartY=0 StartZ=0 EndX=2.10101 EndY=8.75133 EndZ=0
    g2: LineSegment [constr] StartX=0 StartY=0 StartZ=0 EndX=3.44415 EndY=8.31492 EndZ=0
    g3: LineSegment [constr] StartX=0 StartY=0 StartZ=0 EndX=4.70249 EndY=7.67376 EndZ=0
    g4: LineSegment [constr] StartX=0 StartY=0 StartZ=0 EndX=5.84503 EndY=6.84365 EndZ=0
    g5: LineSegment [constr] StartX=0 StartY=0 StartZ=0 EndX=6.84365 EndY=5.84503 EndZ=0
    g6: LineSegment [constr] StartX=0 StartY=0 StartZ=0 EndX=7.67376 EndY=4.70249 EndZ=0
    g7: LineSegment [constr] StartX=0 StartY=0 StartZ=0 EndX=8.31492 EndY=3.44415 EndZ=0
    g8: LineSegment [constr] StartX=0 StartY=0 StartZ=0 EndX=8.75133 EndY=2.10101 EndZ=0
    g9: LineSegment [constr] StartX=0 StartY=0 StartZ=0 EndX=8.97226 EndY=0.706132 EndZ=0
    g10: LineSegment [constr] StartX=0 StartY=0 StartZ=0 EndX=8.97226 EndY=-0.706132 EndZ=0
    g11: LineSegment [constr] StartX=0 StartY=0 StartZ=0 EndX=8.75133 EndY=-2.10101 EndZ=0
    g12: LineSegment [constr] StartX=0 StartY=0 StartZ=0 EndX=8.31492 EndY=-3.44415 EndZ=0
    g13: LineSegment [constr] StartX=0 StartY=0 StartZ=0 EndX=7.67376 EndY=-4.70249 EndZ=0
    g14: LineSegment [constr] StartX=0 StartY=0 StartZ=0 EndX=6.84365 EndY=-5.84503 EndZ=0
    g15: LineSegment [constr] StartX=0 StartY=0 StartZ=0 EndX=5.84503 EndY=-6.84365 EndZ=0
    g16: LineSegment [constr] StartX=0 StartY=0 StartZ=0 EndX=4.70249 EndY=-7.67376 EndZ=0
    g17: LineSegment [constr] StartX=0 StartY=0 StartZ=0 EndX=3.44415 EndY=-8.31492 EndZ=0
    g18: LineSegment [constr] StartX=0 StartY=0 StartZ=0 EndX=2.10101 EndY=-8.75133 EndZ=0
    g19: LineSegment [constr] StartX=0 StartY=0 StartZ=0 EndX=0.706132 EndY=-8.97226 EndZ=0
    g20: LineSegment [constr] StartX=0 StartY=0 StartZ=0 EndX=-0.706132 EndY=-8.97226 EndZ=0
    g21: LineSegment [constr] StartX=0 StartY=0 StartZ=0 EndX=-6.84365 EndY=5.84503 EndZ=0
    g22: LineSegment [constr] StartX=0 StartY=0 StartZ=0 EndX=-5.84503 EndY=6.84365 EndZ=0
    g23: LineSegment [constr] StartX=0 StartY=0 StartZ=0 EndX=-4.70249 EndY=7.67376 EndZ=0
    g24: LineSegment [constr] StartX=0 StartY=0 StartZ=0 EndX=-3.44415 EndY=8.31492 EndZ=0
    g25: LineSegment [constr] StartX=0 StartY=0 StartZ=0 EndX=-2.10101 EndY=8.75133 EndZ=0
    g26: LineSegment [constr] StartX=0 StartY=0 StartZ=0 EndX=-8.75133 EndY=2.10101 EndZ=0
    g27: LineSegment [constr] StartX=0 StartY=0 StartZ=0 EndX=-8.97226 EndY=0.706132 EndZ=0
    g28: LineSegment [constr] StartX=0 StartY=0 StartZ=0 EndX=-8.97226 EndY=-0.706132 EndZ=0
    g29: LineSegment [constr] StartX=0 StartY=0 StartZ=0 EndX=-8.75133 EndY=-2.10101 EndZ=0
    g30: LineSegment [constr] StartX=0 StartY=0 StartZ=0 EndX=-8.31492 EndY=-3.44415 EndZ=0
    g31: LineSegment [constr] StartX=0 StartY=0 StartZ=0 EndX=-7.67376 EndY=-4.70249 EndZ=0
    g32: LineSegment [constr] StartX=0 StartY=0 StartZ=0 EndX=-6.84365 EndY=-5.84503 EndZ=0
    g33: LineSegment [constr] StartX=0 StartY=0 StartZ=0 EndX=-5.84503 EndY=-6.84365 EndZ=0
    g34: LineSegment [constr] StartX=0 StartY=0 StartZ=0 EndX=-4.70249 EndY=-7.67376 EndZ=0
    g35: LineSegment [constr] StartX=0 StartY=0 StartZ=0 EndX=-3.44415 EndY=-8.31492 EndZ=0
    g36: LineSegment [constr] StartX=0 StartY=0 StartZ=0 EndX=-2.10101 EndY=-8.75133 EndZ=0
    g37: LineSegment [constr] StartX=0 StartY=0 StartZ=0 EndX=-8.31492 EndY=3.44415 EndZ=0
    g38: LineSegment [constr] StartX=0 StartY=0 StartZ=0 EndX=-7.67376 EndY=4.70249 EndZ=0
    g39: LineSegment [constr] StartX=0 StartY=0 StartZ=0 EndX=-0.706132 EndY=8.97226 EndZ=0
    g40: LineSegment StartX=0.706132 StartY=8.97226 StartZ=0 EndX=-0.706132 EndY=8.97226 EndZ=0
    g41: LineSegment StartX=-0.706132 StartY=8.97226 StartZ=0 EndX=-0.549998 EndY=6.98839 EndZ=0
    g42: LineSegment StartX=-0.549998 StartY=6.98839 StartZ=0 EndX=0.549998 EndY=6.98839 EndZ=0
    g43: LineSegment StartX=0.549998 StartY=6.98839 StartZ=0 EndX=0.706132 EndY=8.97226 EndZ=0
    g44: LineSegment StartX=2.10101 StartY=8.75133 StartZ=0 EndX=1.63645 EndY=6.81631 EndZ=0
    g45: LineSegment StartX=1.63645 StartY=6.81631 StartZ=0 EndX=2.68261 EndY=6.4764 EndZ=0
    g46: LineSegment StartX=2.68261 StartY=6.4764 StartZ=0 EndX=3.44415 EndY=8.31492 EndZ=0
    g47: LineSegment StartX=3.44415 StartY=8.31492 StartZ=0 EndX=2.10101 EndY=8.75133 EndZ=0
    g48: LineSegment StartX=4.70249 StartY=7.67376 StartZ=0 EndX=5.84503 EndY=6.84365 EndZ=0
    g49: LineSegment StartX=5.84503 StartY=6.84365 StartZ=0 EndX=4.55263 EndY=5.33045 EndZ=0
    g50: LineSegment StartX=4.55263 StartY=5.33045 StartZ=0 EndX=3.66271 EndY=5.97701 EndZ=0
    g51: LineSegment StartX=3.66271 StartY=5.97701 StartZ=0 EndX=4.70249 EndY=7.67376 EndZ=0
    g52: LineSegment StartX=6.84365 StartY=5.84503 StartZ=0 EndX=7.67376 EndY=4.70249 EndZ=0
    g53: LineSegment StartX=7.67376 StartY=4.70249 StartZ=0 EndX=5.97701 EndY=3.66271 EndZ=0
    g54: LineSegment StartX=5.97701 StartY=3.66271 StartZ=0 EndX=5.33045 EndY=4.55263 EndZ=0
    g55: LineSegment StartX=5.33045 StartY=4.55263 StartZ=0 EndX=6.84365 EndY=5.84503 EndZ=0
    g56: LineSegment StartX=8.31492 StartY=3.44415 StartZ=0 EndX=8.75133 EndY=2.10101 EndZ=0
    g57: LineSegment StartX=8.75133 StartY=2.10101 StartZ=0 EndX=6.81631 EndY=1.63645 EndZ=0
    g58: LineSegment StartX=6.81631 StartY=1.63645 StartZ=0 EndX=6.4764 EndY=2.68261 EndZ=0
    g59: LineSegment StartX=6.4764 StartY=2.68261 StartZ=0 EndX=8.31492 EndY=3.44415 EndZ=0
    g60: LineSegment StartX=8.97226 StartY=0.706132 StartZ=0 EndX=8.97226 EndY=-0.706132 EndZ=0
    g61: LineSegment StartX=8.97226 StartY=-0.706132 StartZ=0 EndX=6.98839 EndY=-0.549998 EndZ=0
    g62: LineSegment StartX=6.98839 StartY=-0.549998 StartZ=0 EndX=6.98839 EndY=0.549998 EndZ=0
    g63: LineSegment StartX=6.98839 StartY=0.549998 StartZ=0 EndX=8.97226 EndY=0.706132 EndZ=0
    g64: LineSegment StartX=8.75133 StartY=-2.10101 StartZ=0 EndX=8.31492 EndY=-3.44415 EndZ=0
    g65: LineSegment StartX=8.31492 StartY=-3.44415 StartZ=0 EndX=6.4764 EndY=-2.68261 EndZ=0
    g66: LineSegment StartX=6.4764 StartY=-2.68261 StartZ=0 EndX=6.81631 EndY=-1.63645 EndZ=0
    g67: LineSegment StartX=6.81631 StartY=-1.63645 StartZ=0 EndX=8.75133 EndY=-2.10101 EndZ=0
    g68: LineSegment StartX=7.67376 StartY=-4.70249 StartZ=0 EndX=6.84365 EndY=-5.84503 EndZ=0
    g69: LineSegment StartX=6.84365 StartY=-5.84503 StartZ=0 EndX=5.33045 EndY=-4.55263 EndZ=0
    g70: LineSegment StartX=5.33045 StartY=-4.55263 StartZ=0 EndX=5.97701 EndY=-3.66271 EndZ=0
    g71: LineSegment StartX=5.97701 StartY=-3.66271 StartZ=0 EndX=7.67376 EndY=-4.70249 EndZ=0
    g72: LineSegment StartX=5.84503 StartY=-6.84365 StartZ=0 EndX=4.70249 EndY=-7.67376 EndZ=0
    g73: LineSegment StartX=4.70249 StartY=-7.67376 StartZ=0 EndX=3.66271 EndY=-5.97701 EndZ=0
    g74: LineSegment StartX=3.66271 StartY=-5.97701 StartZ=0 EndX=4.55263 EndY=-5.33045 EndZ=0
    g75: LineSegment StartX=4.55263 StartY=-5.33045 StartZ=0 EndX=5.84503 EndY=-6.84365 EndZ=0
    g76: LineSegment StartX=3.44415 StartY=-8.31492 StartZ=0 EndX=2.10101 EndY=-8.75133 EndZ=0
    g77: LineSegment StartX=2.10101 StartY=-8.75133 StartZ=0 EndX=1.63645 EndY=-6.81631 EndZ=0
    g78: LineSegment StartX=1.63645 StartY=-6.81631 StartZ=0 EndX=2.68261 EndY=-6.4764 EndZ=0
    g79: LineSegment StartX=2.68261 StartY=-6.4764 StartZ=0 EndX=3.44415 EndY=-8.31492 EndZ=0
    g80: LineSegment StartX=0.706132 StartY=-8.97226 StartZ=0 EndX=-0.706132 EndY=-8.97226 EndZ=0
    g81: LineSegment StartX=-0.706132 StartY=-8.97226 StartZ=0 EndX=-0.549998 EndY=-6.98839 EndZ=0
    g82: LineSegment StartX=-0.549998 StartY=-6.98839 StartZ=0 EndX=0.549998 EndY=-6.98839 EndZ=0
    g83: LineSegment StartX=0.549998 StartY=-6.98839 StartZ=0 EndX=0.706132 EndY=-8.97226 EndZ=0
    g84: LineSegment StartX=-2.10101 StartY=-8.75133 StartZ=0 EndX=-3.44415 EndY=-8.31492 EndZ=0
    g85: LineSegment StartX=-3.44415 StartY=-8.31492 StartZ=0 EndX=-2.68261 EndY=-6.4764 EndZ=0
    g86: LineSegment StartX=-2.68261 StartY=-6.4764 StartZ=0 EndX=-1.63645 EndY=-6.81631 EndZ=0
    g87: LineSegment StartX=-1.63645 StartY=-6.81631 StartZ=0 EndX=-2.10101 EndY=-8.75133 EndZ=0
    g88: LineSegment StartX=-4.70249 StartY=-7.67376 StartZ=0 EndX=-5.84503 EndY=-6.84365 EndZ=0
    g89: LineSegment StartX=-5.84503 StartY=-6.84365 StartZ=0 EndX=-4.55263 EndY=-5.33045 EndZ=0
    g90: LineSegment StartX=-4.55263 StartY=-5.33045 StartZ=0 EndX=-3.66271 EndY=-5.97701 EndZ=0
    g91: LineSegment StartX=-3.66271 StartY=-5.97701 StartZ=0 EndX=-4.70249 EndY=-7.67376 EndZ=0
    g92: LineSegment StartX=-6.84365 StartY=-5.84503 StartZ=0 EndX=-7.67376 EndY=-4.70249 EndZ=0
    g93: LineSegment StartX=-7.67376 StartY=-4.70249 StartZ=0 EndX=-5.97701 EndY=-3.66271 EndZ=0
    g94: LineSegment StartX=-5.97701 StartY=-3.66271 StartZ=0 EndX=-5.33045 EndY=-4.55263 EndZ=0
    g95: LineSegment StartX=-5.33045 StartY=-4.55263 StartZ=0 EndX=-6.84365 EndY=-5.84503 EndZ=0
    g96: LineSegment StartX=-8.31492 StartY=-3.44415 StartZ=0 EndX=-6.4764 EndY=-2.68261 EndZ=0
    g97: LineSegment StartX=-6.4764 StartY=-2.68261 StartZ=0 EndX=-6.81631 EndY=-1.63645 EndZ=0
    g98: LineSegment StartX=-8.31492 StartY=-3.44415 StartZ=0 EndX=-8.75133 EndY=-2.10101 EndZ=0
    g99: LineSegment StartX=-8.75133 StartY=-2.10101 StartZ=0 EndX=-6.81631 EndY=-1.63645 EndZ=0
    g100: LineSegment StartX=-8.97226 StartY=-0.706132 StartZ=0 EndX=-8.97226 EndY=0.706132 EndZ=0
    g101: LineSegment StartX=-8.97226 StartY=0.706132 StartZ=0 EndX=-6.98839 EndY=0.549998 EndZ=0
    g102: LineSegment StartX=-6.98839 StartY=0.549998 StartZ=0 EndX=-6.98839 EndY=-0.549998 EndZ=0
    g103: LineSegment StartX=-6.98839 StartY=-0.549998 StartZ=0 EndX=-8.97226 EndY=-0.706132 EndZ=0
    g104: LineSegment StartX=-8.75133 StartY=2.10101 StartZ=0 EndX=-8.31492 EndY=3.44415 EndZ=0
    g105: LineSegment StartX=-8.31492 StartY=3.44415 StartZ=0 EndX=-6.4764 EndY=2.68261 EndZ=0
    g106: LineSegment StartX=-6.4764 StartY=2.68261 StartZ=0 EndX=-6.81631 EndY=1.63645 EndZ=0
    g107: LineSegment StartX=-6.81631 StartY=1.63645 StartZ=0 EndX=-8.75133 EndY=2.10101 EndZ=0
    g108: LineSegment StartX=-7.67376 StartY=4.70249 StartZ=0 EndX=-5.97701 EndY=3.66271 EndZ=0
    g109: LineSegment StartX=-5.97701 StartY=3.66271 StartZ=0 EndX=-5.33045 EndY=4.55263 EndZ=0
    g110: LineSegment StartX=-5.33045 StartY=4.55263 StartZ=0 EndX=-6.84365 EndY=5.84503 EndZ=0
    g111: LineSegment StartX=-6.84365 StartY=5.84503 StartZ=0 EndX=-7.67376 EndY=4.70249 EndZ=0
    g112: LineSegment StartX=-5.84503 StartY=6.84365 StartZ=0 EndX=-4.55263 EndY=5.33045 EndZ=0
    g113: LineSegment StartX=-4.55263 StartY=5.33045 StartZ=0 EndX=-3.66271 EndY=5.97701 EndZ=0
    g114: LineSegment StartX=-3.66271 StartY=5.97701 StartZ=0 EndX=-4.70249 EndY=7.67376 EndZ=0
    g115: LineSegment StartX=-4.70249 StartY=7.67376 StartZ=0 EndX=-5.84503 EndY=6.84365 EndZ=0
    g116: LineSegment StartX=-3.44415 StartY=8.31492 StartZ=0 EndX=-2.68261 EndY=6.4764 EndZ=0
    g117: LineSegment StartX=-2.68261 StartY=6.4764 StartZ=0 EndX=-1.63645 EndY=6.81631 EndZ=0
    g118: LineSegment StartX=-1.63645 StartY=6.81631 StartZ=0 EndX=-2.10101 EndY=8.75133 EndZ=0
    g119: LineSegment StartX=-2.10101 StartY=8.75133 StartZ=0 EndX=-3.44415 EndY=8.31492 EndZ=0
  constraints (320):
    c: PointOnObject(g25,g-4)
    c: PointOnObject(g24,g-4)
    c: PointOnObject(g23,g-4)
    c: PointOnObject(g22,g-4)
    c: PointOnObject(g21,g-4)
    c: PointOnObject(g38,g-4)
    c: PointOnObject(g37,g-4)
    c: Coincident(g34,g-1)
    c: Coincident(g33,g34)
    c: Coincident(g32,g33)
    c: Coincident(g31,g32)
    c: Coincident(g29,g31)
    c: Coincident(g28,g29)
    c: Coincident(g27,g28)
    c: Coincident(g37,g27)
    c: Coincident(g26,g27)
    c: Coincident(g21,g26)
    c: Coincident(g22,g21)
    c: Coincident(g23,g21)
    c: Coincident(g25,g21)
    c: Coincident(g30,g21)
    c: Coincident(g38,g21)
    c: Coincident(g24,g21)
    c: Coincident(g1,g21)
    c: Coincident(g0,g1)
    c: Coincident(g2,g0)
    c: Coincident(g4,g0)
    c: Coincident(g35,g0)
    c: Coincident(g36,g0)
    c: Coincident(g20,g0)
    c: Coincident(g19,g0)
    c: Coincident(g18,g0)
    c: Coincident(g17,g0)
    c: Coincident(g16,g0)
    c: Coincident(g15,g0)
    c: Coincident(g14,g0)
    c: Coincident(g13,g0)
    c: Coincident(g12,g0)
    c: Coincident(g11,g0)
    c: Coincident(g10,g0)
    c: Coincident(g9,g0)
    c: Coincident(g8,g0)
    c: Coincident(g7,g0)
    c: Coincident(g6,g0)
    c: Coincident(g5,g0)
    c: Coincident(g3,g0)
    c: Coincident(g39,g0)
    c: PointOnObject(g39,g-4)
    c: PointOnObject(g0,g-4)
    c: PointOnObject(g1,g-4)
    c: PointOnObject(g2,g-4)
    c: PointOnObject(g3,g-4)
    c: PointOnObject(g4,g-4)
    c: PointOnObject(g5,g-4)
    c: PointOnObject(g6,g-4)
    c: PointOnObject(g7,g-4)
    c: PointOnObject(g8,g-4)
    c: PointOnObject(g9,g-4)
    c: PointOnObject(g10,g-4)
    c: PointOnObject(g11,g-4)
    c: PointOnObject(g12,g-4)
    c: PointOnObject(g13,g-4)
    c: PointOnObject(g14,g-4)
    c: PointOnObject(g15,g-4)
    c: PointOnObject(g16,g-4)
    c: PointOnObject(g17,g-4)
    c: PointOnObject(g18,g-4)
    c: PointOnObject(g19,g-4)
    c: PointOnObject(g20,g-4)
    c: PointOnObject(g36,g-4)
    c: PointOnObject(g35,g-4)
    c: PointOnObject(g34,g-4)
    c: PointOnObject(g33,g-4)
    c: PointOnObject(g32,g-4)
    c: PointOnObject(g31,g-4)
    c: PointOnObject(g30,g-4)
    c: PointOnObject(g29,g-4)
    c: PointOnObject(g28,g-4)
    c: PointOnObject(g27,g-4)
    c: PointOnObject(g26,g-4)
    c: Angle(g-2,g39) = 0.0785398
    c: Angle(g39,g25) = 0.15708
    c: Angle(g25,g24) = 0.15708
    c: Angle(g24,g23) = 0.15708
    c: Angle(g23,g22) = 0.15708
    c: Angle(g22,g21) = 0.15708
    c: Angle(g21,g38) = 0.15708
    c: Angle(g38,g37) = 0.15708
    c: Angle(g37,g26) = 0.15708
    c: Angle(g26,g27) = 0.15708
    c: Angle(g27,g28) = 0.15708
    c: Angle(g28,g29) = 0.15708
    c: Angle(g29,g30) = 0.15708
    c: Angle(g30,g31) = 0.15708
    c: Angle(g31,g32) = 0.15708
    c: Angle(g32,g33) = 0.15708
    c: Angle(g33,g34) = 0.15708
    c: Angle(g34,g35) = 0.15708
    c: Angle(g35,g36) = 0.15708
    c: Angle(g36,g20) = 0.15708
    c: Angle(g20,g19) = 0.15708
    c: Angle(g19,g18) = 0.15708
    c: Angle(g18,g17) = 0.15708
    c: Angle(g17,g16) = 0.15708
    c: Angle(g16,g15) = 0.15708
    c: Angle(g15,g14) = 0.15708
    c: Angle(g14,g13) = 0.15708
    c: Angle(g13,g12) = 0.15708
    c: Angle(g12,g11) = 0.15708
    c: Angle(g11,g10) = 0.15708
    c: Angle(g10,g9) = 0.15708
    c: Angle(g9,g8) = 0.15708
    c: Angle(g8,g7) = 0.15708
    c: Angle(g7,g6) = 0.15708
    c: Angle(g6,g5) = 0.15708
    c: Angle(g5,g4) = 0.15708
    c: Angle(g4,g3) = 0.15708
    c: Angle(g3,g2) = 0.15708
    c: Angle(g2,g1) = 0.15708
    c: Angle(g1,g0) = 0.15708
    c: Coincident(g40,g0)
    c: Coincident(g40,g39)
    c: Coincident(g41,g39)
    c: PointOnObject(g41,g39)
    c: Coincident(g42,g41)
    c: PointOnObject(g42,g0)
    c: Horizontal(g42)
    c: Coincident(g43,g42)
    c: Coincident(g43,g0)
    c: Coincident(g44,g1)
    c: PointOnObject(g44,g1)
    c: Coincident(g45,g44)
    c: PointOnObject(g45,g2)
    c: Coincident(g46,g45)
    c: Coincident(g46,g2)
    c: Coincident(g47,g2)
    c: Coincident(g47,g1)
    c: Coincident(g48,g3)
    c: Coincident(g48,g4)
    c: Coincident(g49,g4)
    c: PointOnObject(g49,g4)
    c: Coincident(g50,g49)
    c: PointOnObject(g50,g3)
    c: Coincident(g51,g50)
    c: Coincident(g51,g48)
    c: Coincident(g52,g5)
    c: Coincident(g52,g6)
    c: Coincident(g53,g6)
    c: PointOnObject(g53,g6)
    c: Coincident(g54,g53)
    c: PointOnObject(g54,g5)
    c: Coincident(g55,g54)
    c: Coincident(g55,g5)
    c: Coincident(g56,g7)
    c: Coincident(g56,g8)
    c: Coincident(g57,g56)
    c: PointOnObject(g57,g8)
    c: Coincident(g58,g57)
    c: PointOnObject(g58,g7)
    c: Coincident(g59,g58)
    c: Coincident(g59,g7)
    c: Coincident(g60,g9)
    c: Coincident(g60,g10)
    c: Coincident(g61,g60)
    c: PointOnObject(g61,g10)
    c: Coincident(g62,g61)
    c: PointOnObject(g62,g9)
    c: Coincident(g63,g62)
    c: Coincident(g63,g9)
    c: Coincident(g64,g11)
    c: Coincident(g64,g12)
    c: Coincident(g65,g12)
    c: PointOnObject(g65,g12)
    c: Coincident(g66,g65)
    c: PointOnObject(g66,g11)
    c: Coincident(g67,g66)
    c: Coincident(g67,g11)
    c: Coincident(g68,g13)
    c: Coincident(g68,g14)
    c: Coincident(g69,g14)
    c: PointOnObject(g69,g14)
    c: Coincident(g70,g69)
    c: PointOnObject(g70,g13)
    c: Coincident(g71,g70)
    c: Coincident(g71,g13)
    c: Coincident(g72,g15)
    c: Coincident(g72,g16)
    c: Coincident(g73,g16)
    c: PointOnObject(g73,g16)
    c: Coincident(g74,g73)
    c: PointOnObject(g74,g15)
    c: Coincident(g75,g74)
    c: Coincident(g75,g72)
    c: Coincident(g76,g17)
    c: Coincident(g76,g18)
    c: Coincident(g77,g18)
    c: PointOnObject(g77,g18)
    c: Coincident(g78,g77)
    c: PointOnObject(g78,g17)
    c: Coincident(g79,g78)
    c: Coincident(g79,g17)
    c: Coincident(g80,g19)
    c: Coincident(g80,g20)
    c: Coincident(g81,g20)
    c: PointOnObject(g81,g20)
    c: Coincident(g82,g81)
    c: PointOnObject(g82,g19)
    c: Horizontal(g82)
    c: Coincident(g83,g82)
    c: Coincident(g83,g19)
    c: Coincident(g84,g36)
    c: Coincident(g84,g35)
    c: Coincident(g85,g35)
    c: PointOnObject(g85,g35)
    c: Coincident(g86,g85)
    c: PointOnObject(g86,g36)
    c: Coincident(g87,g86)
    c: Coincident(g87,g36)
    c: Coincident(g88,g34)
    c: Coincident(g88,g33)
    c: Coincident(g89,g88)
    c: PointOnObject(g89,g33)
    c: Coincident(g90,g89)
    c: PointOnObject(g90,g34)
    c: Coincident(g91,g90)
    c: Coincident(g91,g34)
    c: Coincident(g92,g32)
    c: Coincident(g92,g31)
    c: Coincident(g93,g31)
    c: PointOnObject(g93,g31)
    c: Coincident(g94,g93)
    c: PointOnObject(g94,g32)
    c: Coincident(g95,g94)
    c: Coincident(g95,g32)
    c: Coincident(g96,g30)
    c: PointOnObject(g96,g30)
    c: Coincident(g97,g96)
    c: PointOnObject(g97,g29)
    c: Coincident(g98,g30)
    c: Coincident(g98,g29)
    c: Coincident(g99,g29)
    c: Coincident(g99,g97)
    c: Coincident(g100,g28)
    c: Coincident(g100,g27)
    c: Coincident(g101,g27)
    c: PointOnObject(g101,g27)
    c: Coincident(g102,g101)
    c: PointOnObject(g102,g28)
    c: Coincident(g103,g102)
    c: Coincident(g103,g100)
    c: Coincident(g104,g26)
    c: Coincident(g104,g37)
    c: Coincident(g105,g37)
    c: PointOnObject(g105,g37)
    c: Coincident(g106,g105)
    c: PointOnObject(g106,g26)
    c: Coincident(g107,g106)
    c: Coincident(g107,g104)
    c: Coincident(g108,g38)
    c: PointOnObject(g108,g38)
    c: Coincident(g109,g108)
    c: PointOnObject(g109,g21)
    c: Coincident(g110,g109)
    c: Coincident(g110,g21)
    c: Coincident(g111,g21)
    c: Coincident(g111,g38)
    c: Coincident(g112,g22)
    c: PointOnObject(g112,g22)
    c: Coincident(g113,g112)
    c: PointOnObject(g113,g23)
    c: Coincident(g114,g113)
    c: Coincident(g114,g23)
    c: Coincident(g115,g23)
    c: Coincident(g115,g22)
    c: Coincident(g116,g24)
    c: PointOnObject(g116,g24)
    c: Coincident(g117,g116)
    c: PointOnObject(g117,g25)
    c: Coincident(g118,g117)
    c: Coincident(g118,g25)
    c: Coincident(g119,g25)
    c: Coincident(g119,g24)
    c: PointOnObject(g117,g-3)
    c: PointOnObject(g116,g-3)
    c: PointOnObject(g41,g-3)
    c: PointOnObject(g44,g-3)
    c: PointOnObject(g45,g-3)
    c: PointOnObject(g50,g-3)
    c: PointOnObject(g49,g-3)
    c: PointOnObject(g54,g-3)
    c: PointOnObject(g53,g-3)
    c: PointOnObject(g58,g-3)
    c: PointOnObject(g57,g-3)
    c: PointOnObject(g62,g-3)
    c: PointOnObject(g61,g-3)
    c: PointOnObject(g113,g-3)
    c: PointOnObject(g112,g-3)
    c: PointOnObject(g109,g-3)
    c: PointOnObject(g108,g-3)
    c: PointOnObject(g105,g-3)
    c: PointOnObject(g106,g-3)
    c: PointOnObject(g101,g-3)
    c: PointOnObject(g102,g-3)
    c: PointOnObject(g97,g-3)
    c: PointOnObject(g96,g-3)
    c: PointOnObject(g93,g-3)
    c: PointOnObject(g94,g-3)
    c: PointOnObject(g89,g-3)
    c: PointOnObject(g90,g-3)
    c: PointOnObject(g85,g-3)
    c: PointOnObject(g86,g-3)
    c: PointOnObject(g81,g-3)
    c: PointOnObject(g77,g-3)
    c: PointOnObject(g78,g-3)
    c: PointOnObject(g73,g-3)
    c: PointOnObject(g74,g-3)
    c: PointOnObject(g69,g-3)
    c: PointOnObject(g70,g-3)
    c: PointOnObject(g65,g-3)
    c: PointOnObject(g66,g-3)
FEATURE [PartDesign::Pad] Pad150
  BaseFeature = -> Pocket101
  Direction = (0,1,2e-16)
  Length = 2
  Length2 = 10
  Placement = pos=(0,0,0) rot=(1,0,0;1.5708rad)
  Profile = -> Sketch247
  ReferenceAxis = -> Sketch247 [N_Axis]
  Refine = true
  Reversed = true
  Suppressed = false
  Type = 0
FEATURE [Sketcher::SketchObject] Sketch248
  ArcFitTolerance = 1e-06
  AttachmentSupport = -> [Pad150]
  ExternalGeometry = -> [Pad150]
  FullyConstrained = true
  MakeInternals = false
  MapMode = 5
  Placement = pos=(-1e-16,0,-7e-16) rot=(0.999229,0,-0.03926;3.14159rad)
  sketch-geometry (3):
    g0: LineSegment StartX=7.01 StartY=0 StartZ=0 EndX=9 EndY=6.9e-15 EndZ=0
    g1: LineSegment StartX=9 StartY=6.9e-15 StartZ=0 EndX=9 EndY=0.5 EndZ=0
    g2: LineSegment StartX=9 StartY=0.5 StartZ=0 EndX=7.01 EndY=0 EndZ=0
  constraints (7):
    c: Coincident(g0,g-4)
    c: Coincident(g0,g-4)
    c: Coincident(g1,g0)
    c: PointOnObject(g1,g-3)
    c: Coincident(g2,g1)
    c: Coincident(g2,g0)
    c: DistanceY(g1,g1) = 0.5
FEATURE [PartDesign::SubtractivePipe] SubtractivePipe002
  AuxilleryCurvelinear = true
  AuxillerySpineTangent = false
  BaseFeature = -> Pad150
  Binormal = (0,0,0)
  Mode = 0
  Placement = pos=(0,0,0) rot=(1,0,0;1.5708rad)
  Profile = -> Sketch248
  Refine = true
  Spine = -> Pad150 [Edge2]
  SpineTangent = false
  Suppressed = false
  Transformation = 0
  Transition = 0
FEATURE [Sketcher::SketchObject] Sketch249
  ArcFitTolerance = 1e-06
  AttachmentSupport = -> [SubtractivePipe002]
  FullyConstrained = true
  MakeInternals = false
  MapMode = 5
  Placement = pos=(0,-3.5,0) rot=(1,0,0;1.5708rad)
  sketch-geometry (1):
    g0: Circle CenterX=0 CenterY=0 CenterZ=0 NormalX=0 NormalY=0 NormalZ=1 AngleXU=0 Radius=1
  constraints (2):
    c: Coincident(g0,g-1)
    c: Diameter(g0) = 2
FEATURE [PartDesign::Pocket] Pocket102
  BaseFeature = -> SubtractivePipe002
  Direction = (0,1,-2e-16)
  Length = 5
  Length2 = 5
  Placement = pos=(0,0,0) rot=(1,0,0;1.5708rad)
  Profile = -> Sketch249
  ReferenceAxis = -> Sketch249 [N_Axis]
  Refine = true
  Suppressed = false
  Type = 0
FEATURE [PartDesign::Body] Body007  label="Tire1"
  AllowCompound = false
  Group = -> [Sketch235,Pad145,Sketch236,Pocket097,Sketch237,Pocket098,Sketch238,Pocket099,Sketch239,Pad146,Sketch240,Pad147,Sketch241,Pad148,Sketch242,SubtractivePipe,Chamfer001,Sketch243,Pad149,Sketch244,SubtractivePipe001,Sketch245,Pocket100,Sketch246,Pocket101,Sketch247,Pad150,Sketch248,SubtractivePipe002,Sketch249,Pocket102]
  Origin = -> Origin007
  Placement = pos=(-8.1,-15.75,-6.2) rot=(0,0,1;0rad)
  Tip = -> Pocket102
COMPONENT P11 — same part as P10; its construction recipe is shown at P10.
COMPONENT P12 — same part as P10; its construction recipe is shown at P10.
